FCSTD DOCUMENT  (FreeCAD 0.17R7529 (Git))
Label: extruder_body_hex_v1.4.1
License: CC-BY 3.0
LicenseURL: http://creativecommons.org/licenses/by/3.0/
objects: Sketcher::SketchObject×82, PartDesign::Pocket×48, PartDesign::Pad×30, Part::Feature×10, PartDesign::Chamfer×8, PartDesign::Fillet×4
note: 260 computed .brp shape members not serialized (recipe doc carries the construction recipe); baked Part::Feature solids carry a one-line shape summary decoded from their .brp

FEATURE [Sketcher::SketchObject] Sketch
  MapMode = 5
  sketch-geometry (56):
    g0: LineSegment [constr] StartX=38.5 StartY=7 StartZ=0 EndX=38.5 EndY=0 EndZ=0
    g1: LineSegment StartX=38.5 StartY=0 StartZ=0 EndX=-31.5 EndY=0 EndZ=0
    g2: LineSegment [constr] StartX=-31.5 StartY=0 StartZ=0 EndX=-31.5 EndY=7 EndZ=0
    g3: ArcOfCircle CenterX=-31.5 CenterY=3.5 CenterZ=0 NormalX=0 NormalY=0 NormalZ=1 Radius=3.5 StartAngle=1.5708 EndAngle=4.71239
    g4: LineSegment [constr] StartX=-31.5 StartY=7 StartZ=0 EndX=-35 EndY=7 EndZ=0
    g5: LineSegment [constr] StartX=-35 StartY=7 StartZ=0 EndX=-35 EndY=0 EndZ=0
    g6: LineSegment [constr] StartX=-35 StartY=0 StartZ=0 EndX=-31.5 EndY=0 EndZ=0
    g7: LineSegment [constr] StartX=38.5 StartY=7 StartZ=0 EndX=42 EndY=7 EndZ=0
    g8: LineSegment [constr] StartX=42 StartY=0 StartZ=0 EndX=38.5 EndY=0 EndZ=0
    g9: LineSegment StartX=-31.5 StartY=7 StartZ=0 EndX=-12.5 EndY=7 EndZ=0
    g10: ArcOfCircle CenterX=-12.5 CenterY=13 CenterZ=0 NormalX=0 NormalY=0 NormalZ=1 Radius=6 StartAngle=4.71239 EndAngle=6.28319
    g11: LineSegment [constr] StartX=-6.5 StartY=13 StartZ=0 EndX=-6.5 EndY=27 EndZ=0
    g12: LineSegment StartX=-6.5 StartY=13 StartZ=0 EndX=-14.7934 EndY=17.0274 EndZ=0
    g13: LineSegment StartX=-6.5 StartY=27 StartZ=0 EndX=-12.5 EndY=27 EndZ=0
    g14: ArcOfCircle CenterX=-12.5 CenterY=21.75 CenterZ=0 NormalX=0 NormalY=0 NormalZ=1 Radius=5.25 StartAngle=1.5708 EndAngle=4.26031
    g15: LineSegment StartX=-6.5 StartY=27 StartZ=0 EndX=-6.5 EndY=56 EndZ=0
    g16: ArcOfCircle CenterX=-0.5 CenterY=56 CenterZ=0 NormalX=0 NormalY=0 NormalZ=1 Radius=6 StartAngle=1.5708 EndAngle=3.14159
    g17: LineSegment StartX=-0.499999 StartY=62 StartZ=0 EndX=17.5 EndY=62 EndZ=0
    g18: LineSegment [constr] StartX=17.5 StartY=62 StartZ=0 EndX=17.5 EndY=7 EndZ=0
    g19: LineSegment [constr] StartX=17.5 StartY=7 StartZ=0 EndX=38.5 EndY=7 EndZ=0
    g20: LineSegment StartX=17.5 StartY=26.5 StartZ=0 EndX=28 EndY=26.5 EndZ=0
    g21: LineSegment StartX=28 StartY=26.5 StartZ=0 EndX=34 EndY=7 EndZ=0
    g22: ArcOfCircle CenterX=23.5 CenterY=13 CenterZ=0 NormalX=0 NormalY=0 NormalZ=1 Radius=6 StartAngle=3.14159 EndAngle=4.71239
    g23: ArcOfCircle CenterX=38 CenterY=17.75 CenterZ=0 NormalX=0 NormalY=0 NormalZ=1 Radius=2 StartAngle=1.5708 EndAngle=4.71239
    g24: LineSegment StartX=38 StartY=19.75 StartZ=0 EndX=41 EndY=19.75 EndZ=0
    g25: LineSegment [constr] StartX=41 StartY=19.75 StartZ=0 EndX=41 EndY=15.75 EndZ=0
    g26: LineSegment StartX=41 StartY=15.75 StartZ=0 EndX=38 EndY=15.75 EndZ=0
    g27: LineSegment [constr] StartX=38 StartY=15.75 StartZ=0 EndX=38 EndY=19.75 EndZ=0
    g28: ArcOfCircle CenterX=41 CenterY=17.75 CenterZ=0 NormalX=0 NormalY=0 NormalZ=1 Radius=2 StartAngle=4.71239 EndAngle=7.85398
    g29: LineSegment [constr] StartX=42 StartY=7 StartZ=0 EndX=42 EndY=3.5 EndZ=0
    g30: ArcOfCircle CenterX=38.5 CenterY=3.5 CenterZ=0 NormalX=0 NormalY=0 NormalZ=1 Radius=3.5 StartAngle=4.71239 EndAngle=6.28319
    g31: LineSegment [constr] StartX=42 StartY=3.5 StartZ=0 EndX=42 EndY=0 EndZ=0
    g32: LineSegment StartX=23.5 StartY=7 StartZ=0 EndX=34 EndY=7 EndZ=0
    g33: LineSegment StartX=17.5 StartY=26.5 StartZ=0 EndX=17.5 EndY=13 EndZ=0
    g34: ArcOfCircle CenterX=41 CenterY=17.75 CenterZ=0 NormalX=0 NormalY=0 NormalZ=1 Radius=4.6 StartAngle=6.02539 EndAngle=7.5456
    g35: LineSegment StartX=42 StartY=3.5 StartZ=0 EndX=45.448 EndY=16.5772 EndZ=0
    g36: LineSegment StartX=25.1292 StartY=47.3792 StartZ=0 EndX=28.1292 EndY=47.3792 EndZ=0
    g37: LineSegment [constr] StartX=28.1292 StartY=47.3792 StartZ=0 EndX=28.1292 EndY=43.3792 EndZ=0
    g38: LineSegment StartX=28.1292 StartY=43.3792 StartZ=0 EndX=25.1292 EndY=43.3792 EndZ=0
    g39: LineSegment [constr] StartX=25.1292 StartY=43.3792 StartZ=0 EndX=25.1292 EndY=47.3792 EndZ=0
    g40: ArcOfCircle CenterX=25.1292 CenterY=45.3792 CenterZ=0 NormalX=0 NormalY=0 NormalZ=1 Radius=2 StartAngle=1.5708 EndAngle=4.71239
    g41: ArcOfCircle CenterX=28.1292 CenterY=45.3792 CenterZ=0 NormalX=0 NormalY=0 NormalZ=1 Radius=2 StartAngle=4.71239 EndAngle=7.85398
    g42: LineSegment [constr] StartX=25.1292 StartY=45.3792 StartZ=0 EndX=38 EndY=17.75 EndZ=0
    g43: LineSegment StartX=52.7584 StartY=60.25 StartZ=0 EndX=55.7584 EndY=60.25 EndZ=0
    g44: LineSegment [constr] StartX=55.7584 StartY=60.25 StartZ=0 EndX=55.7584 EndY=56.25 EndZ=0
    g45: LineSegment StartX=55.7584 StartY=56.25 StartZ=0 EndX=52.7584 EndY=56.25 EndZ=0
    g46: LineSegment [constr] StartX=52.7584 StartY=56.25 StartZ=0 EndX=52.7584 EndY=60.25 EndZ=0
    g47: ArcOfCircle CenterX=52.7584 CenterY=58.25 CenterZ=0 NormalX=0 NormalY=0 NormalZ=1 Radius=2 StartAngle=1.5708 EndAngle=4.71239
    g48: ArcOfCircle CenterX=55.7584 CenterY=58.25 CenterZ=0 NormalX=0 NormalY=0 NormalZ=1 Radius=2 StartAngle=4.71239 EndAngle=7.85398
    g49: LineSegment [constr] StartX=25.1292 StartY=45.3792 StartZ=0 EndX=52.7584 EndY=58.25 EndZ=0
    g50: Circle [constr] CenterX=55.7584 CenterY=58.25 CenterZ=0 NormalX=0 NormalY=0 NormalZ=1 Radius=6.3
    g51: ArcOfCircle [constr] CenterX=28.1292 CenterY=45.3792 CenterZ=0 NormalX=0 NormalY=0 NormalZ=1 Radius=4.6 StartAngle=4.51582 EndAngle=6.99813
    g52: Circle [constr] CenterX=47.2887 CenterY=37.492 CenterZ=0 NormalX=0 NormalY=0 NormalZ=1 Radius=16.1194
    g53: ArcOfCircle CenterX=47.2887 CenterY=37.492 CenterZ=0 NormalX=0 NormalY=0 NormalZ=1 Radius=16.1194 StartAngle=1.18339 EndAngle=4.40401
    g54: ArcOfCircle CenterX=55.7584 CenterY=58.25 CenterZ=0 NormalX=0 NormalY=0 NormalZ=1 Radius=6.3 StartAngle=4.32499 EndAngle=7.98709
    g55: ArcOfCircle CenterX=17.5 CenterY=343.976 CenterZ=0 NormalX=0 NormalY=0 NormalZ=1 Radius=281.976 StartAngle=4.71239 EndAngle=4.8455
  constraints (168):
    c: Coincident(g0,g1)
    c: Coincident(g1,g2)
    c: Horizontal(g1)
    c: Vertical(g0)
    c: Vertical(g2)
    c: PointOnObject(g3,g2)
    c: Coincident(g3,g1)
    c: DistanceY(g2,g1) = -7
    c: PointOnObject(g1,g-1)
    c: Coincident(g4,g5)
    c: Coincident(g5,g6)
    c: Horizontal(g4)
    c: Horizontal(g6)
    c: Vertical(g5)
    c: Coincident(g6,g1)
    c: Tangent(g5,g3)
    c: Horizontal(g7)
    c: Horizontal(g8)
    c: Coincident(g8,g0)
    c: DistanceX(g8,g5) = -77
    c: DistanceX(g-1,g8) = 42
    c: Coincident(g9,g2)
    c: Horizontal(g9)
    c: Coincident(g3,g2)
    c: Coincident(g10,g9)
    c: Radius(g10) = 6
    c: Tangent(g10,g9)
    c: Coincident(g11,g10)
    c: Vertical(g11)
    c: Tangent(g10,g11)
    c: Coincident(g12,g10)
    c: Coincident(g13,g11)
    c: Horizontal(g13)
    c: DistanceY(g11,g9) = -20
    c: DistanceX(g-1,g13) = -12.5
    c: DistanceX(g11,g4) = -28.5
    c: Coincident(g14,g13)
    c: Coincident(g14,g12)
    c: Tangent(g14,g13)
    c: Tangent(g14,g12)
    c: Radius(g14) = 5.25
    c: Coincident(g7,g0)
    c: Coincident(g15,g11)
    c: Vertical(g15)
    c: Coincident(g16,g15)
    c: Radius(g16) = 6
    c: Tangent(g16,g15)
    c: Coincident(g17,g16)
    c: Horizontal(g17)
    c: DistanceY(g1,g16) = 62
    c: Vertical(g18)
    c: Coincident(g17,g18)
    c: DistanceX(g18,g7) = 24.5
    c: Coincident(g19,g18)
    c: Coincident(g19,g0)
    c: Horizontal(g19)
    c: PointOnObject(g20,g18)
    c: Horizontal(g20)
    c: Coincident(g21,g20)
    c: PointOnObject(g21,g19)
    c: DistanceX(g21,g7) = 8
    c: PointOnObject(g22,g18)
    c: PointOnObject(g22,g19)
    c: Radius(g22) = 6
    c: Tangent(g22,g19)
    c: Tangent(g22,g18)
    c: DistanceX(g20) = 10.5
    c: DistanceY(g20,g8) = -26.5
    c: Tangent(g16,g17)
    c: Coincident(g4,g2)
    c: Coincident(g24,g25)
    c: Coincident(g25,g26)
    c: Coincident(g26,g27)
    c: Coincident(g27,g24)
    c: Horizontal(g24)
    c: Horizontal(g26)
    c: Vertical(g25)
    c: Vertical(g27)
    c: Coincident(g24,g23)
    c: PointOnObject(g23,g27)
    c: Coincident(g23,g26)
    c: PointOnObject(g28,g25)
    c: Coincident(g28,g24)
    c: Coincident(g28,g25)
    c: DistanceX(g24) = 3
    c: DistanceY(g27) = 4
    c: DistanceY(g25,g8) = -15.75
    c: DistanceX(g-1,g23) = 38
    c: Vertical(g29)
    c: PointOnObject(g30,g0)
    c: Coincident(g30,g0)
    c: Coincident(g30,g29)
    c: Radius(g30) = 3.5
    c: Tangent(g30,g29)
    c: Coincident(g29,g7)
    c: Coincident(g31,g29)
    c: Coincident(g31,g8)
    c: Vertical(g31)
    c: DistanceY(g7,g8) = -7
    c: Coincident(g32,g22)
    c: Coincident(g32,g21)
    c: Coincident(g33,g20)
    c: Coincident(g33,g22)
    c: Coincident(g34,g28)
    c: Radius(g34) = 4.6
    c: Coincident(g35,g29)
    c: Coincident(g35,g34)
    c: Tangent(g35,g34)
    c: Coincident(g36,g37)
    c: Coincident(g37,g38)
    c: Coincident(g38,g39)
    c: Coincident(g39,g36)
    c: Horizontal(g36)
    c: Horizontal(g38)
    c: Vertical(g37)
    c: Vertical(g39)
    c: DistanceY(g39) = 4
    c: DistanceX(g38) = -3
    c: PointOnObject(g40,g39)
    c: Coincident(g40,g36)
    c: Coincident(g40,g38)
    c: PointOnObject(g41,g37)
    c: Coincident(g41,g36)
    c: Coincident(g41,g37)
    c: Coincident(g42,g40)
    c: Coincident(g42,g23)
    c: Coincident(g43,g44)
    c: Coincident(g44,g45)
    c: Coincident(g45,g46)
    c: Coincident(g46,g43)
    c: Horizontal(g43)
    c: Horizontal(g45)
    c: Vertical(g44)
    c: Vertical(g46)
    c: DistanceX(g45) = -3
    c: DistanceY(g46) = 4
    c: PointOnObject(g47,g46)
    c: Coincident(g47,g43)
    c: Coincident(g47,g45)
    c: PointOnObject(g48,g44)
    c: Coincident(g48,g43)
    c: Coincident(g48,g44)
    c: Distance(g42) = 30.48
    c: Coincident(g49,g40)
    c: Coincident(g49,g47)
    c: Perpendicular(g49,g42)
    c: Distance(g49) = 30.48
    c: DistanceY(g-1,g48) = 58.25
    c: Coincident(g50,g48)
    c: Radius(g50) = 6.3
    c: Coincident(g51,g41)
    c: PointOnObject(g51,g49)
    c: PointOnObject(g51,g42)
    c: Radius(g51) = 4.6
    c: Tangent(g52,g50)
    c: Tangent(g52,g34)
    c: Tangent(g52,g51)
    c: Coincident(g53,g52)
    c: PointOnObject(g53,g34)
    c: Equal(g53,g52)
    c: Coincident(g53,g34)
    c: Coincident(g54,g48)
    c: Coincident(g54,g53)
    c: Coincident(g55,g17)
    c: Coincident(g55,g54)
    c: Tangent(g55,g17)
    c: Radius(g54) = 6.3
    c: Tangent(g55,g50)
FEATURE [PartDesign::Pad] Pad
  Length = 9.5
  Length2 = 100
  Profile = -> Sketch
  Type = 0
FEATURE [Sketcher::SketchObject] Sketch001
  ExternalGeometry = -> [Pad]
  MapMode = 5
  Placement = pos=(0,0,9.5) rot=(0,0,1;0rad)
  Support = -> [Pad]
  sketch-geometry (4):
    g0: LineSegment StartX=10.2 StartY=50.625 StartZ=0 EndX=-6.5 EndY=50.625 EndZ=0
    g1: LineSegment StartX=-6.5 StartY=50.625 StartZ=0 EndX=-6.5 EndY=62 EndZ=0
    g2: LineSegment StartX=-6.5 StartY=62 StartZ=0 EndX=10.2 EndY=62 EndZ=0
    g3: LineSegment StartX=10.2 StartY=62 StartZ=0 EndX=10.2 EndY=50.625 EndZ=0
  constraints (12):
    c: Coincident(g0,g1)
    c: Coincident(g1,g2)
    c: Coincident(g2,g3)
    c: Coincident(g3,g0)
    c: Horizontal(g0)
    c: Horizontal(g2)
    c: Vertical(g1)
    c: Vertical(g3)
    c: PointOnObject(g1,g-3)
    c: PointOnObject(g1,g-4)
    c: DistanceX(g0) = -16.7
    c: DistanceY(g3) = -11.375
FEATURE [PartDesign::Pocket] Pocket
  Length = 4
  Profile = -> Sketch001
  Type = 0
FEATURE [Sketcher::SketchObject] Sketch002
  ExternalGeometry = -> [Pocket]
  MapMode = 5
  Placement = pos=(0,0,9.5) rot=(0,0,1;0rad)
  Support = -> [Pocket]
  sketch-geometry (17):
    g0: LineSegment StartX=17.5 StartY=62 StartZ=0 EndX=17.5 EndY=13 EndZ=0
    g1: LineSegment StartX=17.5 StartY=62 StartZ=0 EndX=10.2 EndY=62 EndZ=0
    g2: ArcOfCircle CenterX=23.5 CenterY=13 CenterZ=0 NormalX=0 NormalY=0 NormalZ=1 Radius=6 StartAngle=3.14159 EndAngle=4.71239
    g3: ArcOfCircle CenterX=38.5 CenterY=3.5 CenterZ=0 NormalX=0 NormalY=0 NormalZ=1 Radius=3.5 StartAngle=4.71238 EndAngle=7.85399
    g4: LineSegment StartX=23.5 StartY=7 StartZ=0 EndX=38.5 EndY=7 EndZ=0
    g5: LineSegment [constr] StartX=38.5 StartY=7 StartZ=0 EndX=38.5 EndY=5.6e-11 EndZ=0
    g6: LineSegment StartX=38.5 StartY=5.6e-11 StartZ=0 EndX=-31.5 EndY=0 EndZ=0
    g7: ArcOfCircle CenterX=-31.5 CenterY=3.5 CenterZ=0 NormalX=0 NormalY=0 NormalZ=1 Radius=3.5 StartAngle=1.5708 EndAngle=4.71239
    g8: LineSegment [constr] StartX=-31.5 StartY=7 StartZ=0 EndX=-31.5 EndY=0 EndZ=0
    g9: LineSegment StartX=-12.5 StartY=7 StartZ=0 EndX=-31.5 EndY=7 EndZ=0
    g10: ArcOfCircle CenterX=-12.5 CenterY=13 CenterZ=0 NormalX=0 NormalY=0 NormalZ=1 Radius=6 StartAngle=4.71239 EndAngle=6.28319
    g11: LineSegment StartX=-6.5 StartY=13 StartZ=0 EndX=-14.7934 EndY=17.0274 EndZ=0
    g12: LineSegment StartX=-12.5 StartY=27 StartZ=0 EndX=-6.5 EndY=27 EndZ=0
    g13: LineSegment StartX=-6.5 StartY=27 StartZ=0 EndX=-6.5 EndY=50.625 EndZ=0
    g14: LineSegment StartX=-6.5 StartY=50.625 StartZ=0 EndX=10.2 EndY=50.625 EndZ=0
    g15: LineSegment StartX=10.2 StartY=50.625 StartZ=0 EndX=10.2 EndY=62 EndZ=0
    g16: ArcOfCircle CenterX=-12.5 CenterY=21.75 CenterZ=0 NormalX=0 NormalY=0 NormalZ=1 Radius=5.25 StartAngle=1.5708 EndAngle=4.26031
  constraints (44):
    c: Coincident(g1,g0)
    c: Coincident(g1,g-3)
    c: Coincident(g0,g-3)
    c: Coincident(g0,g-4)
    c: Coincident(g2,g0)
    c: Coincident(g2,g-5)
    c: Tangent(g2,g0)
    c: Coincident(g3,g-6)
    c: Coincident(g4,g2)
    c: Coincident(g4,g3)
    c: Horizontal(g4)
    c: Coincident(g5,g3)
    c: Coincident(g5,g3)
    c: Vertical(g5)
    c: Radius(g3) = 3.5
    c: Coincident(g6,g3)
    c: Coincident(g6,g-6)
    c: Coincident(g7,g6)
    c: Radius(g7) = 3.5
    c: Coincident(g8,g7)
    c: Coincident(g8,g6)
    c: Vertical(g8)
    c: PointOnObject(g7,g8)
    c: Coincident(g9,g7)
    c: Coincident(g9,g-7)
    c: Coincident(g10,g9)
    c: Coincident(g10,g-7)
    c: Coincident(g10,g-7)
    c: Coincident(g11,g10)
    c: Coincident(g13,g12)
    c: Horizontal(g14)
    c: Coincident(g15,g14)
    c: Coincident(g15,g1)
    c: Vertical(g15)
    c: Coincident(g13,g14)
    c: Coincident(g-8,g14)
    c: Coincident(g-9,g12)
    c: Coincident(g11,g-9)
    c: Horizontal(g12)
    c: Coincident(g16,g-9)
    c: Coincident(g16,g12)
    c: Coincident(g11,g16)
    c: Coincident(g12,g-10)
    c: Coincident(g13,g-10)
FEATURE [PartDesign::Pad] Pad001
  Length = 18.5
  Length2 = 100
  Profile = -> Sketch002
  Type = 0
FEATURE [Sketcher::SketchObject] Sketch003
  ExternalGeometry = -> [Pad001]
  MapMode = 5
  Placement = pos=(0,0,28) rot=(0,0,1;0rad)
  Support = -> [Pad001]
  sketch-geometry (1):
    g0: Circle CenterX=4.6 CenterY=38 CenterZ=0 NormalX=0 NormalY=0 NormalZ=1 Radius=4.4
  constraints (3):
    c: DistanceX(g0,g-3) = -11.1
    c: Radius(g0) = 4.4
    c: DistanceY(g-1,g0) = 38
FEATURE [PartDesign::Pocket] Pocket001
  Length = 19.68
  Profile = -> Sketch003
  Type = 0
FEATURE [Sketcher::SketchObject] Sketch004
  ExternalGeometry = -> [Pocket001]
  MapMode = 5
  Placement = pos=(0,0,28) rot=(0,0,1;0rad)
  Support = -> [Pocket001]
  sketch-geometry (10):
    g0: Circle [constr] CenterX=-8.51624 CenterY=37.5745 CenterZ=0 NormalX=0 NormalY=0 NormalZ=1 Radius=11.3
    g1: LineSegment [constr] StartX=0 StartY=34.2576 StartZ=0 EndX=2.286 EndY=34.2576 EndZ=0
    g2: LineSegment StartX=-104.987 StartY=0 StartZ=0 EndX=-84.2591 EndY=0 EndZ=0
    g3: LineSegment [constr] StartX=5.5 StartY=34.2576 StartZ=0 EndX=-6.5 EndY=34.2576 EndZ=0
    g4: LineSegment StartX=5.5 StartY=50.625 StartZ=0 EndX=5.5 EndY=34.2576 EndZ=0
    g5: LineSegment StartX=5.5 StartY=50.625 StartZ=0 EndX=-6.5 EndY=50.625 EndZ=0
    g6: LineSegment [constr] StartX=-6.5 StartY=50.625 StartZ=0 EndX=-6.5 EndY=34.2576 EndZ=0
    g7: LineSegment StartX=2.286 StartY=34.2576 StartZ=0 EndX=5.5 EndY=34.2576 EndZ=0
    g8: ArcOfCircle CenterX=-8.51624 CenterY=37.5745 CenterZ=0 NormalX=0 NormalY=0 NormalZ=1 Radius=11.3 StartAngle=1.39141 EndAngle=5.98527
    g9: LineSegment StartX=-6.5 StartY=50.625 StartZ=0 EndX=-6.5 EndY=48.6931 EndZ=0
  constraints (27):
    c: Radius(g0) = 11.3
    c: PointOnObject(g1,g-2)
    c: Horizontal(g1)
    c: DistanceX(g1) = 2.286
    c: PointOnObject(g1,g0)
    c: Tangent(g2,g-1)
    c: PointOnObject(g-3,g0)
    c: Coincident(g4,g3)
    c: Horizontal(g3)
    c: Vertical(g4)
    c: PointOnObject(g1,g3)
    c: PointOnObject(g1,g-4)
    c: Coincident(g5,g4)
    c: Coincident(g5,g-5)
    c: Coincident(g6,g3)
    c: Coincident(g6,g5)
    c: Vertical(g6)
    c: Coincident(g7,g1)
    c: Coincident(g7,g3)
    c: PointOnObject(g4,g-5)
    c: DistanceX(g4,g-5) = 4.7
    c: Coincident(g8,g0)
    c: PointOnObject(g8,g6)
    c: PointOnObject(g8,g-4)
    c: Coincident(g8,g1)
    c: Coincident(g9,g5)
    c: Coincident(g9,g8)
FEATURE [PartDesign::Pocket] Pocket002
  Length = 18.5
  Profile = -> Sketch004
  Type = 0
FEATURE [Sketcher::SketchObject] Sketch005
  ExternalGeometry = -> [Pocket002]
  MapMode = 5
  Placement = pos=(0,0,28) rot=(0,0,1;0rad)
  Support = -> [Pocket002]
  sketch-geometry (1):
    g0: Circle CenterX=4.6 CenterY=38 CenterZ=0 NormalX=0 NormalY=0 NormalZ=1 Radius=8
  constraints (2):
    c: Coincident(g0,g-3)
    c: Radius(g0) = 8
FEATURE [PartDesign::Pocket] Pocket003
  Length = 9.5
  Profile = -> Sketch005
  Type = 0
FEATURE [Sketcher::SketchObject] Sketch006
  ExternalGeometry = -> [Pocket003]
  MapMode = 5
  Placement = pos=(0,0,28) rot=(0,0,1;0rad)
  Support = -> [Pocket003]
  sketch-geometry (1):
    g0: Circle CenterX=4.6 CenterY=38 CenterZ=0 NormalX=0 NormalY=0 NormalZ=1 Radius=11.3
  constraints (2):
    c: Coincident(g0,g-3)
    c: Radius(g0) = 11.3
FEATURE [PartDesign::Pocket] Pocket004
  Length = 8
  Profile = -> Sketch006
  Type = 0
FEATURE [Sketcher::SketchObject] Sketch007
  ExternalGeometry = -> [Pocket004]
  MapMode = 5
  Placement = pos=(0,0,8.32) rot=(0,0,1;0rad)
  Support = -> [Pocket004]
  sketch-geometry (1):
    g0: Circle CenterX=4.6 CenterY=38 CenterZ=0 NormalX=0 NormalY=0 NormalZ=1 Radius=4
  constraints (2):
    c: Coincident(g0,g-3)
    c: Radius(g0) = 4
FEATURE [PartDesign::Pocket] Pocket005
  Length = 0
  Profile = -> Sketch007
  Type = 1
FEATURE [Sketcher::SketchObject] Sketch008
  ExternalGeometry = -> [Pocket005]
  MapMode = 5
  Placement = pos=(0,0,0) rot=(1,0,0;3.14159rad)
  Support = -> [Pocket005]
  sketch-geometry (1):
    g0: Circle CenterX=4.6 CenterY=-38 CenterZ=0 NormalX=0 NormalY=0 NormalZ=1 Radius=11.3
  constraints (2):
    c: Coincident(g0,g-3)
    c: Radius(g0) = 11.3
FEATURE [PartDesign::Pocket] Pocket006
  Length = 8
  Profile = -> Sketch008
  Type = 0
FEATURE [PartDesign::Chamfer] Chamfer
  Base = -> Pocket006 [Edge22]
  Size = 1
FEATURE [PartDesign::Fillet] Fillet
  Base = -> Chamfer [Edge37,Edge40]
  Radius = 0.5
FEATURE [Sketcher::SketchObject] Sketch009
  ExternalGeometry = -> [Fillet]
  MapMode = 5
  Placement = pos=(0,0,28) rot=(0,0,1;0rad)
  Support = -> [Fillet]
  sketch-geometry (4):
    g0: LineSegment StartX=-6.5 StartY=13 StartZ=0 EndX=-17.75 EndY=13 EndZ=0
    g1: LineSegment StartX=-17.75 StartY=13 StartZ=0 EndX=-17.75 EndY=27 EndZ=0
    g2: LineSegment StartX=-17.75 StartY=27 StartZ=0 EndX=-6.5 EndY=27 EndZ=0
    g3: LineSegment StartX=-6.5 StartY=27 StartZ=0 EndX=-6.5 EndY=13 EndZ=0
  constraints (11):
    c: Coincident(g0,g1)
    c: Coincident(g1,g2)
    c: Coincident(g2,g3)
    c: Coincident(g3,g0)
    c: Horizontal(g0)
    c: Horizontal(g2)
    c: Vertical(g1)
    c: Vertical(g3)
    c: Coincident(g0,g-3)
    c: Tangent(g2,g-4)
    c: Tangent(g1,g-4)
FEATURE [PartDesign::Pocket] Pocket007
  Length = 7.75
  Profile = -> Sketch009
  Type = 0
FEATURE [Sketcher::SketchObject] Sketch010
  ExternalGeometry = -> [Pocket007]
  MapMode = 5
  Placement = pos=(0,0,20.25) rot=(0,0,1;0rad)
  Support = -> [Pocket007]
  sketch-geometry (1):
    g0: Circle CenterX=-12.5 CenterY=21.75 CenterZ=0 NormalX=0 NormalY=0 NormalZ=1 Radius=3.3
  constraints (2):
    c: Coincident(g0,g-3)
    c: Radius(g0) = 3.3
FEATURE [PartDesign::Pocket] Pocket008
  Length = 0.75
  Profile = -> Sketch010
  Type = 0
FEATURE [Sketcher::SketchObject] Sketch011
  ExternalGeometry = -> [Pocket008]
  MapMode = 5
  Placement = pos=(0,0,19.5) rot=(0,0,1;0rad)
  Support = -> [Pocket008]
  sketch-geometry (1):
    g0: Circle CenterX=-12.5 CenterY=21.75 CenterZ=0 NormalX=0 NormalY=0 NormalZ=1 Radius=1.95
  constraints (2):
    c: Coincident(g0,g-3)
    c: Radius(g0) = 1.95
FEATURE [PartDesign::Pocket] Pocket009
  Length = 5
  Profile = -> Sketch011
  Type = 1
FEATURE [Sketcher::SketchObject] Sketch012
  ExternalGeometry = -> [Pocket009]
  MapMode = 5
  Placement = pos=(0,0,0) rot=(1,0,0;3.14159rad)
  Support = -> [Pocket009]
  sketch-geometry (4):
    g0: LineSegment StartX=-6.5 StartY=-13 StartZ=0 EndX=-17.75 EndY=-13 EndZ=0
    g1: LineSegment StartX=-17.75 StartY=-13 StartZ=0 EndX=-17.75 EndY=-27 EndZ=0
    g2: LineSegment StartX=-17.75 StartY=-27 StartZ=0 EndX=-6.5 EndY=-27 EndZ=0
    g3: LineSegment StartX=-6.5 StartY=-27 StartZ=0 EndX=-6.5 EndY=-13 EndZ=0
  constraints (11):
    c: Coincident(g0,g1)
    c: Coincident(g1,g2)
    c: Coincident(g2,g3)
    c: Coincident(g3,g0)
    c: Horizontal(g0)
    c: Horizontal(g2)
    c: Vertical(g1)
    c: Vertical(g3)
    c: Coincident(g0,g-4)
    c: Tangent(g1,g-3)
    c: Coincident(g2,g-5)
FEATURE [PartDesign::Pocket] Pocket010
  Length = 8.32
  Profile = -> Sketch012
  Type = 0
FEATURE [Sketcher::SketchObject] Sketch013
  ExternalGeometry = -> [Pocket010]
  MapMode = 5
  Placement = pos=(0,0,0) rot=(1,0,0;3.14159rad)
  Support = -> [Pocket010]
  sketch-geometry (21):
    g0: ArcOfCircle CenterX=38 CenterY=-17.75 CenterZ=0 NormalX=0 NormalY=0 NormalZ=1 Radius=3.8 StartAngle=1.5708 EndAngle=4.71239
    g1: ArcOfCircle CenterX=41 CenterY=-17.75 CenterZ=0 NormalX=0 NormalY=0 NormalZ=1 Radius=3.8 StartAngle=4.71239 EndAngle=7.85398
    g2: ArcOfCircle CenterX=25.1292 CenterY=-45.3792 CenterZ=0 NormalX=0 NormalY=0 NormalZ=1 Radius=3.8 StartAngle=1.5708 EndAngle=4.71239
    g3: ArcOfCircle CenterX=28.1292 CenterY=-45.3792 CenterZ=0 NormalX=0 NormalY=0 NormalZ=1 Radius=3.8 StartAngle=4.71239 EndAngle=7.85398
    g4: ArcOfCircle CenterX=52.7584 CenterY=-58.25 CenterZ=0 NormalX=0 NormalY=0 NormalZ=1 Radius=3.8 StartAngle=1.5708 EndAngle=4.71239
    g5: ArcOfCircle CenterX=55.7584 CenterY=-58.25 CenterZ=0 NormalX=0 NormalY=0 NormalZ=1 Radius=3.8 StartAngle=4.71239 EndAngle=7.85398
    g6: LineSegment StartX=52.7584 StartY=-54.45 StartZ=0 EndX=55.7584 EndY=-54.45 EndZ=0
    g7: LineSegment StartX=52.7584 StartY=-62.05 StartZ=0 EndX=55.7584 EndY=-62.05 EndZ=0
    g8: LineSegment StartX=25.1292 StartY=-49.1792 StartZ=0 EndX=28.1292 EndY=-49.1792 EndZ=0
    g9: LineSegment StartX=25.1292 StartY=-41.5792 StartZ=0 EndX=28.1292 EndY=-41.5792 EndZ=0
    g10: LineSegment StartX=38 StartY=-21.55 StartZ=0 EndX=41 EndY=-21.55 EndZ=0
    g11: LineSegment StartX=38 StartY=-13.95 StartZ=0 EndX=41 EndY=-13.95 EndZ=0
    g12: LineSegment [constr] StartX=41 StartY=-19.75 StartZ=0 EndX=41 EndY=-21.55 EndZ=0
    g13: LineSegment [constr] StartX=38 StartY=-15.75 StartZ=0 EndX=38 EndY=-13.95 EndZ=0
    g14: LineSegment [constr] StartX=28.1292 StartY=-41.5792 StartZ=0 EndX=28.1292 EndY=-43.3792 EndZ=0
    g15: LineSegment [constr] StartX=25.1292 StartY=-47.3792 StartZ=0 EndX=25.1292 EndY=-49.1792 EndZ=0
    g16: LineSegment [constr] StartX=55.7584 StartY=-54.45 StartZ=0 EndX=55.7584 EndY=-56.25 EndZ=0
    g17: LineSegment [constr] StartX=52.7584 StartY=-60.25 StartZ=0 EndX=52.7584 EndY=-62.05 EndZ=0
    g18: LineSegment [constr] StartX=38 StartY=-19.75 StartZ=0 EndX=38 EndY=-21.55 EndZ=0
    g19: LineSegment [constr] StartX=25.1292 StartY=-43.3792 StartZ=0 EndX=25.1292 EndY=-41.5792 EndZ=0
    g20: LineSegment [constr] StartX=28.1292 StartY=-47.3792 StartZ=0 EndX=28.1292 EndY=-49.1792 EndZ=0
  constraints (54):
    c: Coincident(g0,g-7)
    c: Coincident(g1,g-8)
    c: Coincident(g2,g-3)
    c: Coincident(g3,g-4)
    c: Coincident(g4,g-5)
    c: Coincident(g5,g-6)
    c: Coincident(g6,g4)
    c: Coincident(g6,g5)
    c: Horizontal(g6)
    c: Coincident(g7,g4)
    c: Coincident(g7,g5)
    c: Horizontal(g7)
    c: Coincident(g8,g2)
    c: Coincident(g8,g3)
    c: Horizontal(g8)
    c: Coincident(g9,g2)
    c: Coincident(g9,g3)
    c: Horizontal(g9)
    c: Coincident(g10,g0)
    c: Coincident(g10,g1)
    c: Horizontal(g10)
    c: Coincident(g11,g0)
    c: Coincident(g11,g1)
    c: Horizontal(g11)
    c: Coincident(g12,g-8)
    c: Coincident(g12,g1)
    c: Vertical(g12)
    c: Coincident(g13,g-7)
    c: Coincident(g13,g0)
    c: Vertical(g13)
    c: Coincident(g14,g3)
    c: Vertical(g14)
    c: Coincident(g15,g-3)
    c: Coincident(g15,g2)
    c: Vertical(g15)
    c: Coincident(g14,g-4)
    c: Radius(g1) = 3.8
    c: Radius(g3) = 3.8
    c: Coincident(g16,g5)
    c: Coincident(g16,g-6)
    c: Vertical(g16)
    c: Coincident(g17,g-5)
    c: Coincident(g17,g4)
    c: Vertical(g17)
    c: Radius(g5) = 3.8
    c: Coincident(g18,g-7)
    c: Vertical(g18)
    c: Tangent(g4,g6)
    c: Coincident(g19,g-3)
    c: Coincident(g19,g2)
    c: Vertical(g19)
    c: Coincident(g20,g-4)
    c: Coincident(g20,g3)
    c: Coincident(g18,g0)
FEATURE [PartDesign::Pocket] Pocket011
  Length = 1.5
  Profile = -> Sketch013
  Type = 0
FEATURE [PartDesign::Chamfer] Chamfer001
  Base = -> Pocket011 [Edge173]
  Size = 1.6
FEATURE [PartDesign::Chamfer] Chamfer002
  Base = -> Chamfer001 [Edge169]
  Size = 1.6
FEATURE [PartDesign::Chamfer] Chamfer003
  Base = -> Chamfer002 [Edge73]
  Size = 1.6
FEATURE [Sketcher::SketchObject] Sketch015
  ExternalGeometry = -> [Chamfer003]
  MapMode = 5
  Placement = pos=(10.2,0,0) rot=(0.57735,-0.57735,-0.57735;2.0944rad)
  Support = -> [Chamfer003]
  sketch-geometry (18):
    g0: LineSegment StartX=-55.825 StartY=25.7 StartZ=0 EndX=-50.175 EndY=25.7 EndZ=0
    g1: LineSegment [constr] StartX=-50.175 StartY=25.7 StartZ=0 EndX=-50.175 EndY=18.3 EndZ=0
    g2: LineSegment StartX=-50.175 StartY=18.3 StartZ=0 EndX=-55.825 EndY=18.3 EndZ=0
    g3: LineSegment [constr] StartX=-55.825 StartY=18.3 StartZ=0 EndX=-55.825 EndY=25.7 EndZ=0
    g4: LineSegment StartX=-55.825 StartY=9.9 StartZ=0 EndX=-50.175 EndY=9.9 EndZ=0
    g5: LineSegment [constr] StartX=-50.175 StartY=9.9 StartZ=0 EndX=-50.175 EndY=2.5 EndZ=0
    g6: LineSegment StartX=-50.175 StartY=2.5 StartZ=0 EndX=-55.825 EndY=2.5 EndZ=0
    g7: LineSegment [constr] StartX=-55.825 StartY=2.5 StartZ=0 EndX=-55.825 EndY=9.9 EndZ=0
    g8: LineSegment StartX=-55.825 StartY=25.7 StartZ=0 EndX=-57.675 EndY=22 EndZ=0
    g9: LineSegment StartX=-57.675 StartY=22 StartZ=0 EndX=-55.825 EndY=18.3 EndZ=0
    g10: LineSegment StartX=-50.175 StartY=25.7 StartZ=0 EndX=-48.325 EndY=22 EndZ=0
    g11: LineSegment StartX=-50.175 StartY=18.3 StartZ=0 EndX=-48.325 EndY=22 EndZ=0
    g12: LineSegment [constr] StartX=-57.675 StartY=22 StartZ=0 EndX=-48.325 EndY=22 EndZ=0
    g13: LineSegment StartX=-55.825 StartY=9.9 StartZ=0 EndX=-57.675 EndY=6.2 EndZ=0
    g14: LineSegment StartX=-57.675 StartY=6.2 StartZ=0 EndX=-55.825 EndY=2.5 EndZ=0
    g15: LineSegment StartX=-50.175 StartY=9.9 StartZ=0 EndX=-48.325 EndY=6.2 EndZ=0
    g16: LineSegment StartX=-50.175 StartY=2.5 StartZ=0 EndX=-48.325 EndY=6.2 EndZ=0
    g17: LineSegment [constr] StartX=-57.675 StartY=6.2 StartZ=0 EndX=-48.325 EndY=6.2 EndZ=0
  constraints (48):
    c: Coincident(g0,g1)
    c: Coincident(g1,g2)
    c: Coincident(g2,g3)
    c: Coincident(g3,g0)
    c: Horizontal(g0)
    c: Horizontal(g2)
    c: Vertical(g1)
    c: Vertical(g3)
    c: Coincident(g4,g5)
    c: Coincident(g5,g6)
    c: Coincident(g6,g7)
    c: Coincident(g7,g4)
    c: Horizontal(g4)
    c: Horizontal(g6)
    c: Vertical(g5)
    c: Vertical(g7)
    c: PointOnObject(g2,g7)
    c: PointOnObject(g1,g5)
    c: DistanceY(g0,g-3) = 2.3
    c: Coincident(g8,g0)
    c: Coincident(g9,g8)
    c: Coincident(g9,g2)
    c: Coincident(g10,g0)
    c: Coincident(g11,g1)
    c: Coincident(g11,g10)
    c: Coincident(g12,g8)
    c: Coincident(g12,g10)
    c: Horizontal(g12)
    c: Symmetric(g0,g2,g12)
    c: DistanceX(g12) = 9.35
    c: Parallel(g9,g10)
    c: DistanceX(g2) = -5.65
    c: Coincident(g13,g4)
    c: Coincident(g14,g13)
    c: Coincident(g14,g6)
    c: Coincident(g15,g4)
    c: Coincident(g16,g5)
    c: Coincident(g16,g15)
    c: Coincident(g17,g13)
    c: Coincident(g17,g15)
    c: Horizontal(g17)
    c: Symmetric(g4,g6,g17)
    c: DistanceX(g17) = 9.35
    c: DistanceY(g1) = -7.4
    c: DistanceY(g4,g2) = 8.4
    c: DistanceY(g5) = -7.4
    c: Parallel(g8,g13)
    c: DistanceX(g0,g-3) = -6.175
FEATURE [PartDesign::Pocket] Pocket012
  Length = 5.5
  Profile = -> Sketch015
  Type = 0
FEATURE [Sketcher::SketchObject] Sketch016
  ExternalGeometry = -> [Pocket012]
  MapMode = 5
  Placement = pos=(0,0,0) rot=(1,0,0;3.14159rad)
  Support = -> [Pocket012]
  sketch-geometry (10):
    g0: ArcOfCircle CenterX=28.1292 CenterY=-45.3792 CenterZ=0 NormalX=0 NormalY=0 NormalZ=1 Radius=4 StartAngle=4.71239 EndAngle=7.85398
    g1: ArcOfCircle CenterX=28.1292 CenterY=-45.3792 CenterZ=0 NormalX=0 NormalY=0 NormalZ=1 Radius=3.6 StartAngle=4.71239 EndAngle=7.85398
    g2: LineSegment [constr] StartX=28.1292 StartY=-41.3792 StartZ=0 EndX=28.1292 EndY=-49.3792 EndZ=0
    g3: ArcOfCircle CenterX=25.1292 CenterY=-45.3792 CenterZ=0 NormalX=0 NormalY=0 NormalZ=1 Radius=4 StartAngle=1.5708 EndAngle=4.71239
    g4: ArcOfCircle CenterX=25.1292 CenterY=-45.3792 CenterZ=0 NormalX=0 NormalY=0 NormalZ=1 Radius=3.6 StartAngle=1.5708 EndAngle=4.71239
    g5: LineSegment [constr] StartX=25.1292 StartY=-41.3792 StartZ=0 EndX=25.1292 EndY=-49.3792 EndZ=0
    g6: LineSegment StartX=25.1292 StartY=-41.3792 StartZ=0 EndX=28.1292 EndY=-41.3792 EndZ=0
    g7: LineSegment StartX=25.1292 StartY=-41.7792 StartZ=0 EndX=28.1292 EndY=-41.7792 EndZ=0
    g8: LineSegment StartX=25.1292 StartY=-48.9792 StartZ=0 EndX=28.1292 EndY=-48.9792 EndZ=0
    g9: LineSegment StartX=25.1292 StartY=-49.3792 StartZ=0 EndX=28.1292 EndY=-49.3792 EndZ=0
  constraints (28):
    c: Coincident(g0,g-4)
    c: Coincident(g1,g0)
    c: Coincident(g2,g0)
    c: Coincident(g2,g0)
    c: Vertical(g2)
    c: PointOnObject(g0,g2)
    c: PointOnObject(g1,g2)
    c: PointOnObject(g1,g2)
    c: Coincident(g3,g-3)
    c: Coincident(g4,g3)
    c: Coincident(g5,g3)
    c: Coincident(g5,g3)
    c: Vertical(g5)
    c: PointOnObject(g3,g5)
    c: PointOnObject(g4,g5)
    c: PointOnObject(g4,g5)
    c: Coincident(g6,g3)
    c: Coincident(g6,g0)
    c: Coincident(g7,g4)
    c: Coincident(g7,g1)
    c: Horizontal(g7)
    c: Coincident(g8,g4)
    c: Coincident(g8,g1)
    c: Coincident(g9,g3)
    c: Coincident(g9,g0)
    c: Horizontal(g9)
    c: Radius(g1) = 3.6
    c: Radius(g3) = 4
FEATURE [PartDesign::Pad] Pad002
  Length = 5
  Length2 = 100
  Profile = -> Sketch016
  Reversed = true
  Type = 0
FEATURE [Sketcher::SketchObject] Sketch017
  ExternalGeometry = -> [Pad002]
  MapMode = 5
  Placement = pos=(0,0,0) rot=(1,0,0;3.14159rad)
  Support = -> [Pad002]
  sketch-geometry (10):
    g0: ArcOfCircle CenterX=52.7584 CenterY=-58.25 CenterZ=0 NormalX=0 NormalY=0 NormalZ=1 Radius=4 StartAngle=1.5708 EndAngle=4.71239
    g1: ArcOfCircle CenterX=52.7584 CenterY=-58.25 CenterZ=0 NormalX=0 NormalY=0 NormalZ=1 Radius=3.6 StartAngle=1.5708 EndAngle=4.71239
    g2: ArcOfCircle CenterX=55.7584 CenterY=-58.25 CenterZ=0 NormalX=0 NormalY=0 NormalZ=1 Radius=3.6 StartAngle=4.71239 EndAngle=7.85398
    g3: ArcOfCircle CenterX=55.7584 CenterY=-58.25 CenterZ=0 NormalX=0 NormalY=0 NormalZ=1 Radius=4 StartAngle=4.71239 EndAngle=7.85398
    g4: LineSegment [constr] StartX=52.7584 StartY=-54.25 StartZ=0 EndX=52.7584 EndY=-62.25 EndZ=0
    g5: LineSegment [constr] StartX=55.7584 StartY=-54.25 StartZ=0 EndX=55.7584 EndY=-62.25 EndZ=0
    g6: LineSegment StartX=52.7584 StartY=-54.25 StartZ=0 EndX=55.7584 EndY=-54.25 EndZ=0
    g7: LineSegment StartX=52.7584 StartY=-54.65 StartZ=0 EndX=55.7584 EndY=-54.65 EndZ=0
    g8: LineSegment StartX=52.7584 StartY=-61.85 StartZ=0 EndX=55.7584 EndY=-61.85 EndZ=0
    g9: LineSegment StartX=52.7584 StartY=-62.25 StartZ=0 EndX=55.7584 EndY=-62.25 EndZ=0
  constraints (28):
    c: Coincident(g0,g-3)
    c: Coincident(g1,g0)
    c: Coincident(g2,g-4)
    c: Coincident(g3,g2)
    c: Coincident(g4,g0)
    c: Coincident(g4,g0)
    c: PointOnObject(g0,g4)
    c: Vertical(g4)
    c: PointOnObject(g1,g4)
    c: PointOnObject(g1,g4)
    c: Coincident(g5,g3)
    c: Coincident(g5,g3)
    c: PointOnObject(g2,g5)
    c: PointOnObject(g2,g5)
    c: PointOnObject(g2,g5)
    c: Vertical(g5)
    c: Coincident(g6,g0)
    c: Coincident(g6,g3)
    c: Horizontal(g6)
    c: Coincident(g7,g1)
    c: Coincident(g7,g2)
    c: Horizontal(g7)
    c: Coincident(g8,g1)
    c: Coincident(g8,g2)
    c: Coincident(g9,g0)
    c: Coincident(g9,g3)
    c: Radius(g1) = 3.6
    c: Radius(g3) = 4
FEATURE [PartDesign::Pad] Pad003
  Length = 5
  Length2 = 100
  Profile = -> Sketch017
  Reversed = true
  Type = 0
FEATURE [Sketcher::SketchObject] Sketch018
  ExternalGeometry = -> [Pad003]
  MapMode = 5
  Placement = pos=(0,0,0) rot=(1,0,0;3.14159rad)
  Support = -> [Pad003]
  sketch-geometry (10):
    g0: ArcOfCircle CenterX=38 CenterY=-17.75 CenterZ=0 NormalX=0 NormalY=0 NormalZ=1 Radius=4 StartAngle=1.5708 EndAngle=4.71239
    g1: ArcOfCircle CenterX=41 CenterY=-17.75 CenterZ=0 NormalX=0 NormalY=0 NormalZ=1 Radius=4 StartAngle=4.71239 EndAngle=7.85398
    g2: ArcOfCircle CenterX=38 CenterY=-17.75 CenterZ=0 NormalX=0 NormalY=0 NormalZ=1 Radius=3.6 StartAngle=1.5708 EndAngle=4.71239
    g3: ArcOfCircle CenterX=41 CenterY=-17.75 CenterZ=0 NormalX=0 NormalY=0 NormalZ=1 Radius=3.6 StartAngle=4.71239 EndAngle=7.85398
    g4: LineSegment [constr] StartX=38 StartY=-13.75 StartZ=0 EndX=38 EndY=-21.75 EndZ=0
    g5: LineSegment [constr] StartX=41 StartY=-13.75 StartZ=0 EndX=41 EndY=-21.75 EndZ=0
    g6: LineSegment StartX=38 StartY=-13.75 StartZ=0 EndX=41 EndY=-13.75 EndZ=0
    g7: LineSegment StartX=38 StartY=-14.15 StartZ=0 EndX=41 EndY=-14.15 EndZ=0
    g8: LineSegment StartX=38 StartY=-21.35 StartZ=0 EndX=41 EndY=-21.35 EndZ=0
    g9: LineSegment StartX=38 StartY=-21.75 StartZ=0 EndX=41 EndY=-21.75 EndZ=0
  constraints (28):
    c: Coincident(g0,g-4)
    c: Coincident(g1,g-3)
    c: Coincident(g2,g0)
    c: Coincident(g3,g1)
    c: Coincident(g4,g0)
    c: Coincident(g4,g0)
    c: PointOnObject(g0,g4)
    c: PointOnObject(g2,g4)
    c: PointOnObject(g2,g4)
    c: Coincident(g5,g1)
    c: Coincident(g5,g1)
    c: PointOnObject(g1,g5)
    c: PointOnObject(g3,g5)
    c: PointOnObject(g3,g5)
    c: Coincident(g6,g0)
    c: Coincident(g6,g1)
    c: Horizontal(g6)
    c: Coincident(g7,g2)
    c: Coincident(g7,g3)
    c: Horizontal(g7)
    c: Coincident(g8,g2)
    c: Coincident(g8,g3)
    c: Coincident(g9,g0)
    c: Coincident(g9,g1)
    c: Vertical(g4)
    c: Vertical(g5)
    c: Radius(g3) = 3.6
    c: Radius(g0) = 4
FEATURE [PartDesign::Pad] Pad004
  Length = 5
  Length2 = 100
  Profile = -> Sketch018
  Reversed = true
  Type = 0
FEATURE [Sketcher::SketchObject] Sketch019
  MapMode = 5
  Placement = pos=(-6.5,0,0) rot=(0.57735,-0.57735,-0.57735;2.0944rad)
  Support = -> [Pad004]
  sketch-geometry (5):
    g0: LineSegment StartX=-0.75 StartY=0 StartZ=0 EndX=0 EndY=0 EndZ=0
    g1: LineSegment StartX=0 StartY=0 StartZ=0 EndX=0 EndY=0.893816 EndZ=0
    g2: LineSegment [constr] StartX=0 StartY=0.893816 StartZ=0 EndX=-0.75 EndY=0.893816 EndZ=0
    g3: LineSegment [constr] StartX=-0.75 StartY=0.893816 StartZ=0 EndX=-0.75 EndY=0 EndZ=0
    g4: LineSegment StartX=-0.75 StartY=0 StartZ=0 EndX=0 EndY=0.893816 EndZ=0
  constraints (13):
    c: Coincident(g0,g1)
    c: Coincident(g1,g2)
    c: Coincident(g2,g3)
    c: Coincident(g3,g0)
    c: Horizontal(g0)
    c: Horizontal(g2)
    c: Vertical(g1)
    c: Vertical(g3)
    c: Coincident(g4,g0)
    c: Coincident(g4,g1)
    c: Angle(g0,g4) = 0.872665
    c: DistanceX(g0) = 0.75
    c: Coincident(g0,g-1)
FEATURE [PartDesign::Pocket] Pocket013
  Length = 5
  Midplane = true
  Profile = -> Sketch019
  Type = 1
FEATURE [Sketcher::SketchObject] Sketch020
  ExternalGeometry = -> [Pocket013]
  MapMode = 5
  Placement = pos=(0,0,28) rot=(0,0,1;0rad)
  Support = -> [Pocket013]
  sketch-geometry (6):
    g0: LineSegment StartX=13.9 StartY=62 StartZ=0 EndX=10.2 EndY=62 EndZ=0
    g1: LineSegment StartX=10.2 StartY=62 StartZ=0 EndX=10.2 EndY=50.625 EndZ=0
    g2: LineSegment [constr] StartX=10.2 StartY=50.625 StartZ=0 EndX=13.9 EndY=50.625 EndZ=0
    g3: LineSegment [constr] StartX=13.9 StartY=50.625 StartZ=0 EndX=13.9 EndY=62 EndZ=0
    g4: LineSegment StartX=10.2 StartY=50.625 StartZ=0 EndX=13.9 EndY=57.0336 EndZ=0
    g5: LineSegment StartX=13.9 StartY=57.0336 StartZ=0 EndX=13.9 EndY=62 EndZ=0
  constraints (15):
    c: Coincident(g0,g1)
    c: Coincident(g1,g2)
    c: Coincident(g3,g0)
    c: Horizontal(g0)
    c: Horizontal(g2)
    c: Vertical(g1)
    c: Vertical(g3)
    c: Coincident(g1,g-4)
    c: Coincident(g0,g-3)
    c: DistanceX(g0,g0) = -3.7
    c: Coincident(g4,g1)
    c: PointOnObject(g4,g3)
    c: Angle(g2,g4) = 1.0472
    c: Coincident(g5,g4)
    c: Coincident(g5,g0)
FEATURE [PartDesign::Pocket] Pocket014
  Length = 24
  Profile = -> Sketch020
  Type = 0
FEATURE [Sketcher::SketchObject] Sketch021
  ExternalGeometry = -> [Pocket014]
  MapMode = 5
  Placement = pos=(0,0,5.5) rot=(0,0,1;0rad)
  Support = -> [Pocket014]
  sketch-geometry (4):
    g0: LineSegment StartX=-6.5 StartY=50.625 StartZ=0 EndX=10.2 EndY=50.625 EndZ=0
    g1: LineSegment StartX=10.2 StartY=50.625 StartZ=0 EndX=10.2 EndY=62 EndZ=0
    g2: LineSegment StartX=10.2 StartY=62 StartZ=0 EndX=-6.5 EndY=62 EndZ=0
    g3: LineSegment StartX=-6.5 StartY=62 StartZ=0 EndX=-6.5 EndY=50.625 EndZ=0
  constraints (11):
    c: Coincident(g0,g1)
    c: Coincident(g1,g2)
    c: Coincident(g2,g3)
    c: Coincident(g3,g0)
    c: Horizontal(g0)
    c: Horizontal(g2)
    c: Vertical(g1)
    c: Vertical(g3)
    c: Coincident(g0,g-4)
    c: PointOnObject(g1,g-3)
    c: Coincident(g1,g-5)
FEATURE [PartDesign::Pocket] Pocket015
  Length = 1.5
  Profile = -> Sketch021
  Type = 0
FEATURE [Sketcher::SketchObject] Sketch022
  ExternalGeometry = -> [Pocket015]
  MapMode = 5
  Placement = pos=(-14.2713,8.2395,0) rot=(-0.377965,0.654654,0.654654;3.86433rad)
  Support = -> [Pocket015]
  sketch-geometry (21):
    g0: LineSegment StartX=-53.9702 StartY=24.2 StartZ=0 EndX=-51.3149 EndY=24.2 EndZ=0
    g1: LineSegment [constr] StartX=-51.3149 StartY=24.2 StartZ=0 EndX=-51.3149 EndY=19.8 EndZ=0
    g2: LineSegment StartX=-51.3149 StartY=19.8 StartZ=0 EndX=-53.9702 EndY=19.8 EndZ=0
    g3: LineSegment [constr] StartX=-53.9702 StartY=19.8 StartZ=0 EndX=-53.9702 EndY=24.2 EndZ=0
    g4: LineSegment StartX=-53.9702 StartY=8.4 StartZ=0 EndX=-51.3149 EndY=8.4 EndZ=0
    g5: LineSegment [constr] StartX=-51.3149 StartY=8.4 StartZ=0 EndX=-51.3149 EndY=4 EndZ=0
    g6: LineSegment StartX=-51.3149 StartY=4 StartZ=0 EndX=-53.9702 EndY=4 EndZ=0
    g7: LineSegment [constr] StartX=-53.9702 StartY=4 StartZ=0 EndX=-53.9702 EndY=8.4 EndZ=0
    g8: LineSegment StartX=-53.9702 StartY=8.4 StartZ=0 EndX=-55.2404 EndY=6.2 EndZ=0
    g9: LineSegment StartX=-55.2404 StartY=6.2 StartZ=0 EndX=-53.9702 EndY=4 EndZ=0
    g10: LineSegment StartX=-51.3149 StartY=8.4 StartZ=0 EndX=-50.0447 EndY=6.2 EndZ=0
    g11: LineSegment StartX=-50.0447 StartY=6.2 StartZ=0 EndX=-51.3149 EndY=4 EndZ=0
    g12: LineSegment [constr] StartX=-55.2404 StartY=6.2 StartZ=0 EndX=-50.0447 EndY=6.2 EndZ=0
    g13: LineSegment StartX=-53.9702 StartY=24.2 StartZ=0 EndX=-55.2404 EndY=22 EndZ=0
    g14: LineSegment StartX=-55.2404 StartY=22 StartZ=0 EndX=-53.9702 EndY=19.8 EndZ=0
    g15: LineSegment StartX=-51.3149 StartY=24.2 StartZ=0 EndX=-50.0447 EndY=22 EndZ=0
    g16: LineSegment StartX=-51.3149 StartY=19.8 StartZ=0 EndX=-50.0447 EndY=22 EndZ=0
    g17: LineSegment [constr] StartX=-55.2404 StartY=22 StartZ=0 EndX=-50.0447 EndY=22 EndZ=0
    g18: LineSegment [constr] StartX=-56.898 StartY=22 StartZ=0 EndX=-55.2404 EndY=22 EndZ=0
    g19: LineSegment [constr] StartX=-56.898 StartY=6.2 StartZ=0 EndX=-55.2404 EndY=6.2 EndZ=0
    g20: LineSegment [constr] StartX=-52.6425 StartY=24.2 StartZ=0 EndX=-52.6425 EndY=19.8 EndZ=0
  constraints (56):
    c: Coincident(g0,g1)
    c: Coincident(g1,g2)
    c: Coincident(g2,g3)
    c: Coincident(g3,g0)
    c: Horizontal(g0)
    c: Horizontal(g2)
    c: Vertical(g1)
    c: Vertical(g3)
    c: Coincident(g4,g5)
    c: Coincident(g5,g6)
    c: Coincident(g6,g7)
    c: Coincident(g7,g4)
    c: Horizontal(g4)
    c: Horizontal(g6)
    c: Vertical(g5)
    c: Vertical(g7)
    c: Coincident(g9,g8)
    c: Coincident(g9,g6)
    c: Coincident(g10,g4)
    c: Coincident(g11,g10)
    c: Coincident(g11,g5)
    c: Coincident(g8,g4)
    c: Coincident(g12,g8)
    c: Coincident(g12,g10)
    c: Horizontal(g12)
    c: Symmetric(g4,g6,g12)
    c: Coincident(g13,g0)
    c: Coincident(g14,g13)
    c: Coincident(g14,g2)
    c: Coincident(g15,g0)
    c: Coincident(g16,g1)
    c: Coincident(g16,g15)
    c: Coincident(g17,g13)
    c: Coincident(g17,g15)
    c: Horizontal(g17)
    c: Symmetric(g2,g0,g17)
    c: Parallel(g15,g14)
    c: Parallel(g8,g11)
    c: Parallel(g8,g13)
    c: PointOnObject(g1,g5)
    c: PointOnObject(g2,g7)
    c: Distance(g1) = 4.4
    c: DistanceY(g5) = -4.4
    c: Distance(g10,g4) = 4.5
    c: Angle(g9,g8) = 2.0944
    c: Coincident(g18,g-3)
    c: Coincident(g18,g13)
    c: Horizontal(g18)
    c: Coincident(g19,g-4)
    c: Coincident(g19,g8)
    c: Horizontal(g19)
    c: PointOnObject(g20,g0)
    c: PointOnObject(g20,g2)
    c: Vertical(g20)
    c: Symmetric(g0,g0,g20)
    c: Distance(g-5,g20) = 3.7
FEATURE [PartDesign::Pocket] Pocket016
  Length = 11
  Profile = -> Sketch022
  Type = 0
FEATURE [Sketcher::SketchObject] Sketch023
  ExternalGeometry = -> [Pocket016]
  MapMode = 5
  Placement = pos=(0,0,28) rot=(0,0,1;0rad)
  Support = -> [Pocket016]
  sketch-geometry (6):
    g0: LineSegment [constr] StartX=13.9 StartY=55.8212 StartZ=0 EndX=13.9 EndY=62 EndZ=0
    g1: LineSegment StartX=13.9 StartY=62 StartZ=0 EndX=5.5 EndY=62 EndZ=0
    g2: LineSegment StartX=5.5 StartY=62 StartZ=0 EndX=5.5 EndY=50.625 EndZ=0
    g3: LineSegment StartX=10.9 StartY=50.625 StartZ=0 EndX=13.9 EndY=55.8212 EndZ=0
    g4: LineSegment StartX=13.9 StartY=55.8212 StartZ=0 EndX=13.9 EndY=62 EndZ=0
    g5: LineSegment StartX=5.5 StartY=50.625 StartZ=0 EndX=10.9 EndY=50.625 EndZ=0
  constraints (16):
    c: Coincident(g0,g1)
    c: Coincident(g1,g2)
    c: Horizontal(g1)
    c: Vertical(g0)
    c: Vertical(g2)
    c: Coincident(g0,g-3)
    c: PointOnObject(g3,g0)
    c: Coincident(g4,g0)
    c: Coincident(g4,g3)
    c: DistanceX(g3,g0) = 3
    c: Coincident(g5,g2)
    c: Coincident(g3,g5)
    c: Horizontal(g5)
    c: Coincident(g2,g-4)
    c: Angle(g3,g5) = 2.0944
    c: Coincident(g0,g3)
FEATURE [PartDesign::Pad] Pad005
  Length = 24
  Length2 = 100
  Profile = -> Sketch023
  Reversed = true
  Type = 0
FEATURE [Sketcher::SketchObject] Sketch024
  ExternalGeometry = -> [Pad005]
  MapMode = 5
  Placement = pos=(-13.7463,7.93641,0) rot=(0.774597,0.447214,0.447214;1.82348rad)
  Support = -> [Pad005]
  sketch-geometry (6):
    g0: LineSegment StartX=50.0447 StartY=22 StartZ=0 EndX=51.3148 EndY=24.2 EndZ=0
    g1: LineSegment StartX=51.3148 StartY=24.2 StartZ=0 EndX=53.9702 EndY=24.2 EndZ=0
    g2: LineSegment StartX=53.9702 StartY=24.2 StartZ=0 EndX=55.2404 EndY=22 EndZ=0
    g3: LineSegment StartX=55.2404 StartY=22 StartZ=0 EndX=53.9702 EndY=19.8 EndZ=0
    g4: LineSegment StartX=53.9702 StartY=19.8 StartZ=0 EndX=51.3148 EndY=19.8 EndZ=0
    g5: LineSegment StartX=51.3148 StartY=19.8 StartZ=0 EndX=50.0447 EndY=22 EndZ=0
  constraints (14):
    c: Coincident(g-4,g0)
    c: Coincident(g0,g1)
    c: Horizontal(g1)
    c: Coincident(g1,g2)
    c: Coincident(g2,g-3)
    c: Coincident(g2,g3)
    c: Coincident(g3,g4)
    c: Horizontal(g4)
    c: Coincident(g4,g5)
    c: Coincident(g5,g0)
    c: Coincident(g0,g-4)
    c: Coincident(g1,g-3)
    c: Coincident(g4,g-5)
    c: Coincident(g3,g-5)
FEATURE [PartDesign::Pocket] Pocket017
  Length = 13
  Profile = -> Sketch024
  Type = 0
FEATURE [Sketcher::SketchObject] Sketch025
  ExternalGeometry = -> [Pocket017]
  MapMode = 5
  Placement = pos=(-13.7463,7.93641,0) rot=(0.774597,0.447214,0.447214;1.82348rad)
  Support = -> [Pocket017]
  sketch-geometry (11):
    g0: LineSegment [constr] StartX=51.3148 StartY=19.8 StartZ=0 EndX=51.3148 EndY=8.4 EndZ=0
    g1: LineSegment [constr] StartX=53.9702 StartY=19.8 StartZ=0 EndX=53.9702 EndY=8.4 EndZ=0
    g2: LineSegment StartX=51.3148 StartY=8.4 StartZ=0 EndX=53.9702 EndY=8.4 EndZ=0
    g3: LineSegment StartX=53.9702 StartY=8.4 StartZ=0 EndX=55.2404 EndY=6.2 EndZ=0
    g4: LineSegment StartX=55.2404 StartY=6.2 StartZ=0 EndX=53.9702 EndY=4 EndZ=0
    g5: LineSegment StartX=53.9702 StartY=4 StartZ=0 EndX=51.3148 EndY=4 EndZ=0
    g6: LineSegment StartX=51.3148 StartY=4 StartZ=0 EndX=50.0447 EndY=6.2 EndZ=0
    g7: LineSegment StartX=50.0447 StartY=6.2 StartZ=0 EndX=51.3148 EndY=8.4 EndZ=0
    g8: LineSegment [constr] StartX=50.0447 StartY=6.2 StartZ=0 EndX=55.2404 EndY=6.2 EndZ=0
    g9: LineSegment [constr] StartX=51.3148 StartY=8.4 StartZ=0 EndX=51.3148 EndY=4 EndZ=0
    g10: LineSegment [constr] StartX=53.9702 StartY=8.4 StartZ=0 EndX=53.9702 EndY=4 EndZ=0
  constraints (28):
    c: Coincident(g0,g-5)
    c: Vertical(g0)
    c: Coincident(g1,g-5)
    c: Vertical(g1)
    c: Coincident(g0,g2)
    c: Coincident(g2,g1)
    c: Horizontal(g2)
    c: Coincident(g2,g3)
    c: Coincident(g3,g4)
    c: Coincident(g4,g5)
    c: Horizontal(g5)
    c: Coincident(g5,g6)
    c: Coincident(g6,g7)
    c: Coincident(g7,g0)
    c: Coincident(g8,g6)
    c: Coincident(g8,g3)
    c: Horizontal(g8)
    c: Coincident(g9,g0)
    c: Coincident(g9,g5)
    c: Vertical(g9)
    c: Coincident(g10,g1)
    c: Coincident(g10,g4)
    c: Vertical(g10)
    c: Symmetric(g5,g0,g8)
    c: Parallel(g7,g-3)
    c: Parallel(g3,g-4)
    c: DistanceY(g10) = -4.4
    c: DistanceY(g1) = -11.4
FEATURE [PartDesign::Pocket] Pocket018
  Length = 10
  Profile = -> Sketch025
  Type = 0
FEATURE [Sketcher::SketchObject] Sketch026
  ExternalGeometry = -> [Pocket018]
  MapMode = 5
  Placement = pos=(5.5,0,0) rot=(0.57735,-0.57735,-0.57735;2.0944rad)
  Support = -> [Pocket018]
  sketch-geometry (9):
    g0: LineSegment StartX=-54.4355 StartY=8.4 StartZ=0 EndX=-52.0917 EndY=8.4 EndZ=0
    g1: LineSegment StartX=-52.0917 StartY=8.4 StartZ=0 EndX=-50.625 EndY=6.2 EndZ=0
    g2: LineSegment StartX=-50.625 StartY=6.2 StartZ=0 EndX=-52.0917 EndY=4 EndZ=0
    g3: LineSegment StartX=-52.0917 StartY=4 StartZ=0 EndX=-54.4355 EndY=4 EndZ=0
    g4: LineSegment StartX=-54.4355 StartY=4 StartZ=0 EndX=-55.9022 EndY=6.2 EndZ=0
    g5: LineSegment StartX=-55.9022 StartY=6.2 StartZ=0 EndX=-54.4355 EndY=8.4 EndZ=0
    g6: LineSegment [constr] StartX=-55.9022 StartY=6.2 StartZ=0 EndX=-50.625 EndY=6.2 EndZ=0
    g7: LineSegment [constr] StartX=-52.0917 StartY=8.4 StartZ=0 EndX=-52.0917 EndY=4 EndZ=0
    g8: LineSegment [constr] StartX=-54.4355 StartY=4 StartZ=0 EndX=-54.4355 EndY=8.4 EndZ=0
  constraints (24):
    c: Horizontal(g0)
    c: Coincident(g0,g1)
    c: Coincident(g1,g2)
    c: Coincident(g2,g3)
    c: Horizontal(g3)
    c: Coincident(g3,g4)
    c: Coincident(g4,g5)
    c: Coincident(g5,g0)
    c: Coincident(g6,g4)
    c: Coincident(g6,g1)
    c: Horizontal(g6)
    c: Coincident(g7,g0)
    c: Coincident(g7,g2)
    c: Vertical(g7)
    c: Symmetric(g2,g0,g6)
    c: PointOnObject(g-3,g0)
    c: PointOnObject(g-4,g3)
    c: Parallel(g1,g-3)
    c: Parallel(g5,g-4)
    c: Coincident(g8,g3)
    c: Coincident(g8,g0)
    c: Vertical(g8)
    c: Distance(g4,g2) = 4.4
    c: PointOnObject(g1,g-5)
FEATURE [PartDesign::Pocket] Pocket019
  Length = 18
  Profile = -> Sketch026
  Type = 0
FEATURE [Sketcher::SketchObject] Sketch027
  ExternalGeometry = -> [Pocket019]
  MapMode = 5
  Placement = pos=(5.5,0,0) rot=(0.57735,-0.57735,-0.57735;2.0944rad)
  Support = -> [Pocket019]
  sketch-geometry (9):
    g0: LineSegment StartX=-55.9022 StartY=22 StartZ=0 EndX=-54.4355 EndY=24.2 EndZ=0
    g1: LineSegment StartX=-54.4355 StartY=24.2 StartZ=0 EndX=-52.0917 EndY=24.2 EndZ=0
    g2: LineSegment StartX=-52.0917 StartY=24.2 StartZ=0 EndX=-50.625 EndY=22 EndZ=0
    g3: LineSegment StartX=-50.625 StartY=22 StartZ=0 EndX=-52.0917 EndY=19.8 EndZ=0
    g4: LineSegment StartX=-52.0917 StartY=19.8 StartZ=0 EndX=-54.4355 EndY=19.8 EndZ=0
    g5: LineSegment StartX=-54.4355 StartY=19.8 StartZ=0 EndX=-55.9022 EndY=22 EndZ=0
    g6: LineSegment [constr] StartX=-55.9022 StartY=22 StartZ=0 EndX=-50.625 EndY=22 EndZ=0
    g7: LineSegment [constr] StartX=-54.4355 StartY=24.2 StartZ=0 EndX=-54.4355 EndY=19.8 EndZ=0
    g8: LineSegment [constr] StartX=-52.0917 StartY=24.2 StartZ=0 EndX=-52.0917 EndY=19.8 EndZ=0
  constraints (24):
    c: Coincident(g0,g1)
    c: Horizontal(g1)
    c: Coincident(g1,g2)
    c: Coincident(g2,g3)
    c: Coincident(g3,g4)
    c: Horizontal(g4)
    c: Coincident(g4,g5)
    c: Coincident(g5,g0)
    c: Coincident(g6,g0)
    c: Coincident(g6,g2)
    c: Horizontal(g6)
    c: Coincident(g7,g0)
    c: Coincident(g7,g4)
    c: Vertical(g7)
    c: Coincident(g8,g1)
    c: Coincident(g8,g3)
    c: Vertical(g8)
    c: Symmetric(g4,g0,g6)
    c: Parallel(g-3,g2)
    c: Parallel(g5,g-3)
    c: PointOnObject(g-3,g1)
    c: PointOnObject(g-4,g4)
    c: Distance(g0,g2) = 4.4
    c: PointOnObject(g2,g-5)
FEATURE [PartDesign::Pocket] Pocket020
  Length = 18
  Profile = -> Sketch027
  Type = 0
FEATURE [Sketcher::SketchObject] Sketch028
  ExternalGeometry = -> [Pocket020]
  MapMode = 5
  Placement = pos=(5.5,0,0) rot=(0.57735,-0.57735,-0.57735;2.0944rad)
  Support = -> [Pocket020]
  sketch-geometry (4):
    g0: LineSegment StartX=-56.0779 StartY=24.2 StartZ=0 EndX=-54.4355 EndY=24.2 EndZ=0
    g1: LineSegment StartX=-54.4355 StartY=24.2 StartZ=0 EndX=-54.4355 EndY=19.8 EndZ=0
    g2: LineSegment StartX=-54.4355 StartY=19.8 StartZ=0 EndX=-56.0779 EndY=19.8 EndZ=0
    g3: LineSegment StartX=-56.0779 StartY=19.8 StartZ=0 EndX=-56.0779 EndY=24.2 EndZ=0
  constraints (10):
    c: Coincident(g0,g1)
    c: Coincident(g1,g2)
    c: Coincident(g2,g3)
    c: Coincident(g3,g0)
    c: Horizontal(g0)
    c: Horizontal(g2)
    c: Vertical(g1)
    c: Vertical(g3)
    c: Coincident(g0,g-3)
    c: Coincident(g-4,g2)
FEATURE [PartDesign::Pocket] Pocket021
  Length = 5
  Profile = -> Sketch028
  Type = 0
FEATURE [Sketcher::SketchObject] Sketch029
  ExternalGeometry = -> [Pocket021]
  MapMode = 5
  Placement = pos=(5.5,0,0) rot=(0.57735,-0.57735,-0.57735;2.0944rad)
  Support = -> [Pocket021]
  sketch-geometry (4):
    g0: LineSegment StartX=-56.0779 StartY=8.4 StartZ=0 EndX=-54.4355 EndY=8.4 EndZ=0
    g1: LineSegment StartX=-54.4355 StartY=8.4 StartZ=0 EndX=-54.4355 EndY=4 EndZ=0
    g2: LineSegment StartX=-54.4355 StartY=4 StartZ=0 EndX=-56.0779 EndY=4 EndZ=0
    g3: LineSegment StartX=-56.0779 StartY=4 StartZ=0 EndX=-56.0779 EndY=8.4 EndZ=0
  constraints (10):
    c: Coincident(g0,g1)
    c: Coincident(g1,g2)
    c: Coincident(g2,g3)
    c: Coincident(g3,g0)
    c: Horizontal(g0)
    c: Horizontal(g2)
    c: Vertical(g1)
    c: Vertical(g3)
    c: Coincident(g0,g-4)
    c: Coincident(g1,g-3)
FEATURE [PartDesign::Pocket] Pocket022
  Length = 5
  Profile = -> Sketch029
  Type = 0
FEATURE [Sketcher::SketchObject] Sketch030
  ExternalGeometry = -> [Pocket022]
  MapMode = 5
  Placement = pos=(15.7,0,0) rot=(0.57735,-0.57735,-0.57735;2.0944rad)
  Support = -> [Pocket022]
  sketch-geometry (4):
    g0: LineSegment StartX=-52.0917 StartY=4 StartZ=0 EndX=-49.4791 EndY=4 EndZ=0
    g1: LineSegment StartX=-49.4791 StartY=4 StartZ=0 EndX=-49.4791 EndY=8.4 EndZ=0
    g2: LineSegment StartX=-49.4791 StartY=8.4 StartZ=0 EndX=-52.0917 EndY=8.4 EndZ=0
    g3: LineSegment StartX=-52.0917 StartY=8.4 StartZ=0 EndX=-52.0917 EndY=4 EndZ=0
  constraints (11):
    c: Coincident(g0,g1)
    c: Coincident(g1,g2)
    c: Coincident(g2,g3)
    c: Coincident(g3,g0)
    c: Horizontal(g0)
    c: Horizontal(g2)
    c: Vertical(g1)
    c: Vertical(g3)
    c: PointOnObject(g1,g-4)
    c: Coincident(g-5,g0)
    c: Coincident(g0,g-3)
FEATURE [PartDesign::Pocket] Pocket023
  Length = 7.8
  Profile = -> Sketch030
  Type = 0
FEATURE [Sketcher::SketchObject] Sketch031
  ExternalGeometry = -> [Pocket023]
  MapMode = 5
  Placement = pos=(0,62,0) rot=(0,0.707107,0.707107;3.14159rad)
  Support = -> [Pocket023]
  sketch-geometry (7):
    g0: LineSegment [constr] StartX=-13.9 StartY=25 StartZ=0 EndX=-10.2 EndY=25 EndZ=0
    g1: LineSegment StartX=-10.2 StartY=25 StartZ=0 EndX=-10.2 EndY=18.3 EndZ=0
    g2: LineSegment StartX=-10.2 StartY=18.3 StartZ=0 EndX=-13.9 EndY=18.3 EndZ=0
    g3: LineSegment StartX=-13.9 StartY=18.3 StartZ=0 EndX=-13.9 EndY=25 EndZ=0
    g4: LineSegment StartX=-13.9 StartY=25 StartZ=0 EndX=-13.1448 EndY=25.9 EndZ=0
    g5: LineSegment StartX=-13.1448 StartY=25.9 StartZ=0 EndX=-10.9552 EndY=25.9 EndZ=0
    g6: LineSegment StartX=-10.9552 StartY=25.9 StartZ=0 EndX=-10.2 EndY=25 EndZ=0
  constraints (20):
    c: Coincident(g0,g1)
    c: Coincident(g1,g2)
    c: Coincident(g2,g3)
    c: Coincident(g3,g0)
    c: Horizontal(g0)
    c: Horizontal(g2)
    c: Vertical(g1)
    c: Vertical(g3)
    c: Coincident(g4,g0)
    c: Coincident(g5,g4)
    c: Horizontal(g5)
    c: Coincident(g6,g0)
    c: Angle(g6,g0) = 0.872665
    c: Angle(g0,g4) = 0.872665
    c: DistanceY(g0,g4) = 0.9
    c: Coincident(g5,g6)
    c: DistanceX(g2) = -3.7
    c: DistanceX(g0,g-3) = 4.7
    c: DistanceY(g3) = 6.7
    c: DistanceY(g4,g-3) = 2.1
FEATURE [PartDesign::Pocket] Pocket024
  Length = 11.8
  Profile = -> Sketch031
  Type = 0
FEATURE [Sketcher::SketchObject] Sketch032
  ExternalGeometry = -> [Pocket024]
  MapMode = 5
  Placement = pos=(0,62,0) rot=(0,0.707107,0.707107;3.14159rad)
  Support = -> [Pocket024]
  sketch-geometry (7):
    g0: LineSegment [constr] StartX=-13.9 StartY=9.2 StartZ=0 EndX=-10.2 EndY=9.2 EndZ=0
    g1: LineSegment StartX=-10.2 StartY=9.2 StartZ=0 EndX=-10.2 EndY=2.5 EndZ=0
    g2: LineSegment StartX=-10.2 StartY=2.5 StartZ=0 EndX=-13.9 EndY=2.5 EndZ=0
    g3: LineSegment StartX=-13.9 StartY=2.5 StartZ=0 EndX=-13.9 EndY=9.2 EndZ=0
    g4: LineSegment StartX=-13.1448 StartY=10.1 StartZ=0 EndX=-10.9552 EndY=10.1 EndZ=0
    g5: LineSegment StartX=-10.9552 StartY=10.1 StartZ=0 EndX=-10.2 EndY=9.2 EndZ=0
    g6: LineSegment StartX=-13.1448 StartY=10.1 StartZ=0 EndX=-13.9 EndY=9.2 EndZ=0
  constraints (20):
    c: Coincident(g0,g1)
    c: Coincident(g1,g2)
    c: Coincident(g2,g3)
    c: Coincident(g3,g0)
    c: Horizontal(g0)
    c: Horizontal(g2)
    c: Vertical(g1)
    c: Vertical(g3)
    c: PointOnObject(g-3,g1)
    c: PointOnObject(g-3,g3)
    c: Horizontal(g4)
    c: Coincident(g5,g4)
    c: Coincident(g5,g0)
    c: Coincident(g6,g4)
    c: Coincident(g6,g0)
    c: Angle(g0,g6) = 0.872665
    c: Angle(g5,g0) = 0.872665
    c: DistanceY(g4,g0) = -0.9
    c: DistanceY(g2,g0) = 6.7
    c: DistanceY(g-3,g4) = -8.2
FEATURE [PartDesign::Pocket] Pocket025
  Length = 11.8
  Profile = -> Sketch032
  Type = 0
FEATURE [Sketcher::SketchObject] Sketch033
  MapMode = 5
  Placement = pos=(0,2.5e-11,0) rot=(1,0,0;1.5708rad)
  Support = -> [Pocket025]
  sketch-geometry (6):
    g0: Circle [constr] CenterX=0 CenterY=14 CenterZ=0 NormalX=0 NormalY=0 NormalZ=1 Radius=2.05
    g1: LineSegment StartX=-1.57039 StartY=15.3177 StartZ=0 EndX=-0.578336 EndY=16.5 EndZ=0
    g2: LineSegment StartX=-0.578336 StartY=16.5 StartZ=0 EndX=0.578336 EndY=16.5 EndZ=0
    g3: LineSegment StartX=0.578336 StartY=16.5 StartZ=0 EndX=1.57039 EndY=15.3177 EndZ=0
    g4: LineSegment [constr] StartX=0 StartY=14 StartZ=0 EndX=0 EndY=16.5 EndZ=0
    g5: ArcOfCircle CenterX=0 CenterY=14 CenterZ=0 NormalX=0 NormalY=0 NormalZ=1 Radius=2.05 StartAngle=2.44346 EndAngle=6.98132
  constraints (18):
    c: Radius(g0) = 2.05
    c: DistanceY(g0) = 14
    c: PointOnObject(g1,g0)
    c: Tangent(g1,g0)
    c: Coincident(g2,g1)
    c: Horizontal(g2)
    c: Coincident(g3,g2)
    c: PointOnObject(g3,g0)
    c: Tangent(g3,g0)
    c: Coincident(g4,g0)
    c: PointOnObject(g4,g2)
    c: Symmetric(g2,g1,g4)
    c: DistanceY(g2,g0) = -2.5
    c: Angle(g2,g3) = 2.26893
    c: PointOnObject(g0,g-2)
    c: Coincident(g5,g0)
    c: Coincident(g5,g3)
    c: Coincident(g5,g1)
FEATURE [PartDesign::Pocket] Pocket026
  Length = 36
  Profile = -> Sketch033
  Type = 0
FEATURE [Sketcher::SketchObject] Sketch034
  ExternalGeometry = -> [Pocket026]
  MapMode = 5
  Placement = pos=(0,2.5e-11,0) rot=(1,0,0;1.5708rad)
  Support = -> [Pocket026]
  sketch-geometry (2):
    g0: Circle CenterX=-25 CenterY=14 CenterZ=0 NormalX=0 NormalY=0 NormalZ=1 Radius=2.35
    g1: LineSegment [constr] StartX=-25 StartY=14 StartZ=0 EndX=0 EndY=14 EndZ=0
  constraints (5):
    c: Radius(g0) = 2.35
    c: Coincident(g1,g-3)
    c: Horizontal(g1)
    c: DistanceX(g1) = 25
    c: Coincident(g0,g1)
FEATURE [PartDesign::Pocket] Pocket027
  Length = 9
  Profile = -> Sketch034
  Type = 0
FEATURE [Sketcher::SketchObject] Sketch035
  ExternalGeometry = -> [Pocket027]
  MapMode = 5
  Placement = pos=(0,2.5e-11,0) rot=(1,0,0;1.5708rad)
  Support = -> [Pocket027]
  sketch-geometry (2):
    g0: Circle CenterX=25 CenterY=14 CenterZ=0 NormalX=0 NormalY=0 NormalZ=1 Radius=2.35
    g1: LineSegment [constr] StartX=0 StartY=14 StartZ=0 EndX=25 EndY=14 EndZ=0
  constraints (5):
    c: Coincident(g1,g-3)
    c: Coincident(g1,g0)
    c: Horizontal(g1)
    c: Radius(g0) = 2.35
    c: DistanceX(g1) = 25
FEATURE [PartDesign::Pocket] Pocket028
  Length = 7
  Profile = -> Sketch035
  Type = 0
FEATURE [Sketcher::SketchObject] Sketch036
  ExternalGeometry = -> [Pocket028]
  MapMode = 5
  Placement = pos=(0,7,0) rot=(0,0.707107,0.707107;3.14159rad)
  Support = -> [Pocket028]
  sketch-geometry (13):
    g0: LineSegment [constr] StartX=-27.1016 StartY=17.64 StartZ=0 EndX=-22.8984 EndY=17.64 EndZ=0
    g1: LineSegment [constr] StartX=-22.8984 StartY=17.64 StartZ=0 EndX=-22.8984 EndY=10.36 EndZ=0
    g2: LineSegment StartX=-22.8984 StartY=10.36 StartZ=0 EndX=-27.1016 EndY=10.36 EndZ=0
    g3: LineSegment [constr] StartX=-27.1016 StartY=10.36 StartZ=0 EndX=-27.1016 EndY=17.64 EndZ=0
    g4: LineSegment StartX=-27.1016 StartY=17.64 StartZ=0 EndX=-29.2031 EndY=14 EndZ=0
    g5: LineSegment StartX=-29.2031 StartY=14 StartZ=0 EndX=-27.1016 EndY=10.36 EndZ=0
    g6: LineSegment StartX=-22.8984 StartY=17.64 StartZ=0 EndX=-20.7969 EndY=14 EndZ=0
    g7: LineSegment StartX=-20.7969 StartY=14 StartZ=0 EndX=-22.8984 EndY=10.36 EndZ=0
    g8: LineSegment [constr] StartX=-29.2031 StartY=14 StartZ=0 EndX=-20.7969 EndY=14 EndZ=0
    g9: LineSegment [constr] StartX=-25 StartY=14 StartZ=0 EndX=-25 EndY=17.64 EndZ=0
    g10: LineSegment StartX=-27.1016 StartY=17.64 StartZ=0 EndX=-26.8129 EndY=18.14 EndZ=0
    g11: LineSegment StartX=-26.8129 StartY=18.14 StartZ=0 EndX=-23.1871 EndY=18.14 EndZ=0
    g12: LineSegment StartX=-23.1871 StartY=18.14 StartZ=0 EndX=-22.8984 EndY=17.64 EndZ=0
  constraints (35):
    c: Coincident(g0,g1)
    c: Coincident(g1,g2)
    c: Coincident(g2,g3)
    c: Coincident(g3,g0)
    c: Horizontal(g0)
    c: Horizontal(g2)
    c: Vertical(g1)
    c: Vertical(g3)
    c: Coincident(g0,g4)
    c: Coincident(g4,g5)
    c: Coincident(g5,g2)
    c: Coincident(g0,g6)
    c: Coincident(g6,g7)
    c: Coincident(g7,g1)
    c: Coincident(g8,g4)
    c: Horizontal(g8)
    c: Coincident(g6,g8)
    c: Symmetric(g2,g0,g8)
    c: Angle(g5,g4) = 2.0944
    c: Angle(g6,g7) = 2.0944
    c: PointOnObject(g-3,g8)
    c: PointOnObject(g9,g0)
    c: Vertical(g9)
    c: Coincident(g9,g-3)
    c: DistanceY(g0,g2) = -7.28
    c: Distance(g4,g1) = 7.28
    c: Symmetric(g0,g0,g9)
    c: Coincident(g10,g0)
    c: Coincident(g11,g10)
    c: Horizontal(g11)
    c: Coincident(g12,g11)
    c: Coincident(g12,g0)
    c: Parallel(g12,g6)
    c: Parallel(g10,g4)
    c: DistanceY(g10,g0) = -0.5
FEATURE [PartDesign::Pocket] Pocket029
  Length = 3.5
  Profile = -> Sketch036
  Type = 0
FEATURE [Sketcher::SketchObject] Sketch037
  ExternalGeometry = -> [Pocket029]
  MapMode = 5
  Placement = pos=(0,7,0) rot=(0,0.707107,0.707107;3.14159rad)
  Support = -> [Pocket029]
  sketch-geometry (13):
    g0: LineSegment [constr] StartX=22.8984 StartY=17.64 StartZ=0 EndX=27.1016 EndY=17.64 EndZ=0
    g1: LineSegment [constr] StartX=27.1016 StartY=17.64 StartZ=0 EndX=27.1016 EndY=10.36 EndZ=0
    g2: LineSegment StartX=27.1016 StartY=10.36 StartZ=0 EndX=22.8984 EndY=10.36 EndZ=0
    g3: LineSegment [constr] StartX=22.8984 StartY=10.36 StartZ=0 EndX=22.8984 EndY=17.64 EndZ=0
    g4: LineSegment [constr] StartX=25 StartY=14 StartZ=0 EndX=25 EndY=17.64 EndZ=0
    g5: LineSegment StartX=22.8984 StartY=17.64 StartZ=0 EndX=20.7969 EndY=14 EndZ=0
    g6: LineSegment StartX=20.7969 StartY=14 StartZ=0 EndX=22.8984 EndY=10.36 EndZ=0
    g7: LineSegment StartX=27.1016 StartY=17.64 StartZ=0 EndX=29.2031 EndY=14 EndZ=0
    g8: LineSegment StartX=29.2031 StartY=14 StartZ=0 EndX=27.1016 EndY=10.36 EndZ=0
    g9: LineSegment [constr] StartX=20.7969 StartY=14 StartZ=0 EndX=29.2031 EndY=14 EndZ=0
    g10: LineSegment StartX=22.8984 StartY=17.64 StartZ=0 EndX=23.1871 EndY=18.14 EndZ=0
    g11: LineSegment StartX=27.1016 StartY=17.64 StartZ=0 EndX=26.8129 EndY=18.14 EndZ=0
    g12: LineSegment StartX=23.1871 StartY=18.14 StartZ=0 EndX=26.8129 EndY=18.14 EndZ=0
  constraints (35):
    c: Coincident(g0,g1)
    c: Coincident(g1,g2)
    c: Coincident(g2,g3)
    c: Coincident(g3,g0)
    c: Horizontal(g0)
    c: Horizontal(g2)
    c: Vertical(g1)
    c: Vertical(g3)
    c: Coincident(g4,g-3)
    c: PointOnObject(g4,g0)
    c: Vertical(g4)
    c: Symmetric(g0,g0,g4)
    c: Coincident(g0,g5)
    c: Coincident(g5,g6)
    c: Coincident(g6,g2)
    c: Coincident(g0,g7)
    c: Coincident(g7,g8)
    c: Coincident(g8,g1)
    c: Coincident(g9,g5)
    c: Coincident(g9,g7)
    c: Horizontal(g9)
    c: PointOnObject(g4,g9)
    c: Angle(g6,g5) = 2.0944
    c: Angle(g7,g8) = 2.0944
    c: DistanceY(g3) = 7.28
    c: Distance(g0,g7) = 7.28
    c: Parallel(g5,g8)
    c: Coincident(g10,g0)
    c: Coincident(g11,g0)
    c: Coincident(g12,g10)
    c: Coincident(g12,g11)
    c: Horizontal(g12)
    c: Parallel(g11,g7)
    c: Parallel(g10,g5)
    c: DistanceY(g10,g0) = -0.5
FEATURE [PartDesign::Pocket] Pocket030
  Length = 3.5
  Profile = -> Sketch037
  Type = 0
FEATURE [Sketcher::SketchObject] Sketch038
  ExternalGeometry = -> [Pocket030]
  MapMode = 5
  Placement = pos=(0,0,8) rot=(1,0,0;3.14159rad)
  Support = -> [Pocket030]
  sketch-geometry (2):
    g0: Circle CenterX=4.6 CenterY=-38 CenterZ=0 NormalX=0 NormalY=0 NormalZ=1 Radius=4.4
    g1: Circle CenterX=4.6 CenterY=-38 CenterZ=0 NormalX=0 NormalY=0 NormalZ=1 Radius=4
  constraints (4):
    c: Coincident(g0,g-3)
    c: Coincident(g1,g0)
    c: Equal(g-3,g1)
    c: Radius(g0) = 4.4
FEATURE [PartDesign::Pocket] Pocket031
  Length = 1
  Profile = -> Sketch038
  Type = 0
FEATURE [Sketcher::SketchObject] Sketch040
  ExternalGeometry = -> [Pocket031]
  MapMode = 5
  Placement = pos=(0,0,8.32) rot=(1,0,0;3.14159rad)
  Support = -> [Pocket031]
  sketch-geometry (4):
    g0: LineSegment StartX=-6.5 StartY=-13 StartZ=0 EndX=-18.5 EndY=-13 EndZ=0
    g1: LineSegment StartX=-18.5 StartY=-13 StartZ=0 EndX=-18.5 EndY=-27 EndZ=0
    g2: LineSegment StartX=-18.5 StartY=-27 StartZ=0 EndX=-6.5 EndY=-27 EndZ=0
    g3: LineSegment StartX=-6.5 StartY=-27 StartZ=0 EndX=-6.5 EndY=-13 EndZ=0
  constraints (11):
    c: Coincident(g0,g1)
    c: Coincident(g1,g2)
    c: Coincident(g2,g3)
    c: Coincident(g3,g0)
    c: Horizontal(g0)
    c: Horizontal(g2)
    c: Vertical(g1)
    c: Vertical(g3)
    c: Coincident(g0,g-3)
    c: Coincident(g2,g-3)
    c: DistanceX(g0) = -12
FEATURE [PartDesign::Pocket] Pocket032
  Length = 0.32
  Profile = -> Sketch040
  Type = 0
FEATURE [Part::Feature] Pocket032001  label="Pocket033"
  shape: bbox 97.06 x 64.55 x 28 mm, 171 faces (baked)
FEATURE [Sketcher::SketchObject] Sketch042
  ExternalGeometry = -> [Pocket032001]
  MapMode = 5
  Placement = pos=(0,0,8.64) rot=(1,0,0;3.14159rad)
  Support = -> [Pocket032001]
  sketch-geometry (2):
    g0: Circle CenterX=-12.5 CenterY=-21.75 CenterZ=0 NormalX=0 NormalY=0 NormalZ=1 Radius=2.35
    g1: Circle CenterX=-12.5 CenterY=-21.75 CenterZ=0 NormalX=0 NormalY=0 NormalZ=1 Radius=1.95
  constraints (4):
    c: Coincident(g0,g-3)
    c: Coincident(g1,g0)
    c: Radius(g1) = 1.95
    c: Radius(g0) = 2.35
FEATURE [PartDesign::Pad] Pad006
  Length = 8.6
  Length2 = 100
  Profile = -> Sketch042
  Type = 0
FEATURE [Sketcher::SketchObject] Sketch043
  ExternalGeometry = -> [Pad006]
  MapMode = 5
  Placement = pos=(0,0,8.64) rot=(1,0,0;3.14159rad)
  Support = -> [Pad006]
  sketch-geometry (11):
    g0: ArcOfCircle CenterX=-12.5 CenterY=-21.75 CenterZ=0 NormalX=0 NormalY=0 NormalZ=1 Radius=5.25 StartAngle=2.02287 EndAngle=4.71239
    g1: LineSegment StartX=-14.7934 StartY=-17.0274 StartZ=0 EndX=-7.67473 EndY=-13.5705 EndZ=0
    g2: LineSegment StartX=-12.5 StartY=-27 StartZ=0 EndX=-7.5 EndY=-27 EndZ=0
    g3: LineSegment StartX=-7.5 StartY=-27 StartZ=0 EndX=-7.5 EndY=-26.6 EndZ=0
    g4: LineSegment StartX=-7.5 StartY=-26.6 StartZ=0 EndX=-12.5 EndY=-26.6 EndZ=0
    g5: LineSegment [constr] StartX=-12.5 StartY=-26.6 StartZ=0 EndX=-12.5 EndY=-27 EndZ=0
    g6: ArcOfCircle CenterX=-12.5 CenterY=-21.75 CenterZ=0 NormalX=0 NormalY=0 NormalZ=1 Radius=4.85 StartAngle=2.02287 EndAngle=4.71239
    g7: LineSegment [constr] StartX=-14.7934 StartY=-17.0274 StartZ=0 EndX=-14.6186 EndY=-17.3872 EndZ=0
    g8: LineSegment StartX=-7.67473 StartY=-13.5705 StartZ=0 EndX=-7.5 EndY=-13.9303 EndZ=0
    g9: LineSegment StartX=-14.6186 StartY=-17.3872 StartZ=0 EndX=-7.5 EndY=-13.9303 EndZ=0
    g10: LineSegment [constr] StartX=-7.5 StartY=-26.6 StartZ=0 EndX=-7.5 EndY=-13.9303 EndZ=0
  constraints (31):
    c: Coincident(g0,g-3)
    c: Horizontal(g2)
    c: PointOnObject(g-4,g2)
    c: Coincident(g1,g0)
    c: PointOnObject(g-4,g1)
    c: Radius(g0) = 5.25
    c: Coincident(g2,g0)
    c: Coincident(g0,g-5)
    c: Coincident(g3,g2)
    c: Vertical(g3)
    c: Coincident(g4,g3)
    c: Horizontal(g4)
    c: Coincident(g5,g4)
    c: Vertical(g5)
    c: Coincident(g5,g0)
    c: DistanceY(g3) = 0.4
    c: DistanceX(g2,g-4) = 1
    c: Coincident(g6,g0)
    c: Coincident(g6,g4)
    c: Coincident(g7,g0)
    c: Coincident(g7,g6)
    c: Coincident(g8,g1)
    c: Perpendicular(g8,g1)
    c: Coincident(g9,g6)
    c: Coincident(g9,g8)
    c: Perpendicular(g9,g8)
    c: Distance(g8) = 0.4
    c: Perpendicular(g7,g9)
    c: Coincident(g10,g3)
    c: Vertical(g10)
    c: Coincident(g8,g10)
FEATURE [PartDesign::Pad] Pad007
  Length = 8.6
  Length2 = 100
  Profile = -> Sketch043
  Type = 0
FEATURE [Sketcher::SketchObject] Sketch044
  ExternalGeometry = -> [Pad007]
  MapMode = 5
  Placement = pos=(0,0,0.0399993) rot=(1,0,0;3.14159rad)
  Support = -> [Pad007]
  sketch-geometry (12):
    g0: LineSegment StartX=-8.41568 StartY=-27 StartZ=0 EndX=-7.5 EndY=-27 EndZ=0
    g1: LineSegment StartX=-7.5 StartY=-27 StartZ=0 EndX=-7.5 EndY=-13.9303 EndZ=0
    g2: LineSegment StartX=-7.5 StartY=-13.9303 StartZ=0 EndX=-8.41568 EndY=-13.9303 EndZ=0
    g3: LineSegment [constr] StartX=-8.41568 StartY=-13.9303 StartZ=0 EndX=-8.41568 EndY=-27 EndZ=0
    g4: LineSegment [constr] StartX=-7.5 StartY=-20.75 StartZ=0 EndX=-17.6539 EndY=-20.75 EndZ=0
    g5: LineSegment StartX=-17.6539 StartY=-20.75 StartZ=0 EndX=-17.6539 EndY=-22.75 EndZ=0
    g6: LineSegment [constr] StartX=-17.6539 StartY=-22.75 StartZ=0 EndX=-7.5 EndY=-22.75 EndZ=0
    g7: LineSegment StartX=-7.5 StartY=-22.75 StartZ=0 EndX=-7.5 EndY=-20.75 EndZ=0
    g8: LineSegment StartX=-17.6539 StartY=-20.75 StartZ=0 EndX=-8.41568 EndY=-20.75 EndZ=0
    g9: LineSegment StartX=-17.6539 StartY=-22.75 StartZ=0 EndX=-8.41568 EndY=-22.75 EndZ=0
    g10: LineSegment StartX=-8.41568 StartY=-20.75 StartZ=0 EndX=-8.41568 EndY=-13.9303 EndZ=0
    g11: LineSegment StartX=-8.41568 StartY=-22.75 StartZ=0 EndX=-8.41568 EndY=-27 EndZ=0
  constraints (33):
    c: Coincident(g0,g1)
    c: Coincident(g1,g2)
    c: Coincident(g2,g3)
    c: Coincident(g3,g0)
    c: Horizontal(g0)
    c: Horizontal(g2)
    c: Vertical(g1)
    c: Vertical(g3)
    c: PointOnObject(g0,g-3)
    c: Coincident(g1,g-4)
    c: PointOnObject(g2,g-5)
    c: Coincident(g4,g5)
    c: Coincident(g5,g6)
    c: Coincident(g6,g7)
    c: Coincident(g7,g4)
    c: Horizontal(g4)
    c: Horizontal(g6)
    c: Vertical(g5)
    c: Vertical(g7)
    c: PointOnObject(g4,g1)
    c: PointOnObject(g4,g-6)
    c: PointOnObject(g5,g-6)
    c: DistanceY(g5) = -2
    c: Coincident(g8,g4)
    c: Coincident(g9,g5)
    c: PointOnObject(g9,g3)
    c: PointOnObject(g9,g6)
    c: PointOnObject(g8,g3)
    c: PointOnObject(g8,g4)
    c: Coincident(g10,g8)
    c: Coincident(g10,g2)
    c: Coincident(g11,g9)
    c: Coincident(g11,g0)
FEATURE [PartDesign::Pad] Pad008
  Length = 2
  Length2 = 100
  Profile = -> Sketch044
  Reversed = true
  Type = 0
FEATURE [Sketcher::SketchObject] Sketch045
  ExternalGeometry = -> [Pad008]
  MapMode = 5
  Placement = pos=(0,0,8) rot=(1,0,0;3.14159rad)
  Support = -> [Pad008]
  sketch-geometry (2):
    g0: Circle CenterX=4.6 CenterY=-38 CenterZ=0 NormalX=0 NormalY=0 NormalZ=1 Radius=4.8
    g1: Circle CenterX=4.6 CenterY=-38 CenterZ=0 NormalX=0 NormalY=0 NormalZ=1 Radius=4.4
  constraints (4):
    c: Coincident(g0,g-3)
    c: Coincident(g1,g0)
    c: Radius(g1) = 4.4
    c: Radius(g0) = 4.8
FEATURE [PartDesign::Pad] Pad009
  Length = 8
  Length2 = 100
  Profile = -> Sketch045
  Type = 0
FEATURE [Sketcher::SketchObject] Sketch046
  ExternalGeometry = -> [Pad009]
  MapMode = 5
  Placement = pos=(0,0,8) rot=(1,0,0;3.14159rad)
  Support = -> [Pad009]
  sketch-geometry (5):
    g0: LineSegment StartX=-6.5 StartY=-34.2 StartZ=0 EndX=-6.1 EndY=-34.2 EndZ=0
    g1: LineSegment StartX=-6.1 StartY=-34.2 StartZ=0 EndX=-6.1 EndY=-41.8 EndZ=0
    g2: LineSegment StartX=-6.1 StartY=-41.8 StartZ=0 EndX=-6.5 EndY=-41.8 EndZ=0
    g3: LineSegment StartX=-6.5 StartY=-41.8 StartZ=0 EndX=-6.5 EndY=-34.2 EndZ=0
    g4: LineSegment [constr] StartX=4.6 StartY=-38 StartZ=0 EndX=-6.5 EndY=-38 EndZ=0
  constraints (15):
    c: Coincident(g0,g1)
    c: Coincident(g1,g2)
    c: Coincident(g2,g3)
    c: Coincident(g3,g0)
    c: Horizontal(g0)
    c: Horizontal(g2)
    c: Vertical(g1)
    c: Vertical(g3)
    c: PointOnObject(g0,g-3)
    c: Coincident(g4,g-4)
    c: PointOnObject(g4,g3)
    c: Horizontal(g4)
    c: Symmetric(g0,g2,g4)
    c: DistanceX(g0) = 0.4
    c: DistanceY(g1) = -7.6
FEATURE [PartDesign::Pad] Pad010
  Length = 8
  Length2 = 100
  Profile = -> Sketch046
  Type = 0
FEATURE [Sketcher::SketchObject] Sketch047
  ExternalGeometry = -> [Pad010]
  MapMode = 5
  Placement = pos=(0,0,0) rot=(1,0,0;3.14159rad)
  Support = -> [Pad010]
  sketch-geometry (5):
    g0: LineSegment StartX=-6.5 StartY=-36.5 StartZ=0 EndX=14.4 EndY=-36.5 EndZ=0
    g1: LineSegment StartX=14.4 StartY=-36.5 StartZ=0 EndX=14.4 EndY=-39.5 EndZ=0
    g2: LineSegment StartX=14.4 StartY=-39.5 StartZ=0 EndX=-6.5 EndY=-39.5 EndZ=0
    g3: LineSegment StartX=-6.5 StartY=-39.5 StartZ=0 EndX=-6.5 EndY=-36.5 EndZ=0
    g4: LineSegment [constr] StartX=-6.5 StartY=-38 StartZ=0 EndX=4.6 EndY=-38 EndZ=0
  constraints (15):
    c: Coincident(g0,g1)
    c: Coincident(g1,g2)
    c: Coincident(g2,g3)
    c: Coincident(g3,g0)
    c: Horizontal(g0)
    c: Horizontal(g2)
    c: Vertical(g1)
    c: Vertical(g3)
    c: PointOnObject(g0,g-4)
    c: Coincident(g4,g-3)
    c: Horizontal(g4)
    c: PointOnObject(g4,g-4)
    c: Symmetric(g0,g2,g4)
    c: DistanceY(g1) = -3
    c: DistanceX(g4,g1) = 9.8
FEATURE [PartDesign::Pad] Pad011
  Length = 2
  Length2 = 100
  Profile = -> Sketch047
  Reversed = true
  Type = 0
FEATURE [Part::Feature] Pad011001  label="Pad012"
  shape: bbox 97.06 x 64.55 x 28 mm, 206 faces (baked)
FEATURE [Sketcher::SketchObject] Sketch048
  ExternalGeometry = -> [Pad011001]
  MapMode = 5
  Placement = pos=(0,0,0) rot=(1,0,0;3.14159rad)
  Support = -> [Pad011001]
  sketch-geometry (2):
    g0: Circle CenterX=4.6 CenterY=-38 CenterZ=0 NormalX=0 NormalY=0 NormalZ=1 Radius=6.2
    g1: Circle CenterX=4.6 CenterY=-38 CenterZ=0 NormalX=0 NormalY=0 NormalZ=1 Radius=6.6
  constraints (4):
    c: Coincident(g0,g-3)
    c: Radius(g0) = 6.2
    c: Coincident(g1,g0)
    c: Radius(g1) = 6.6
FEATURE [PartDesign::Pad] Pad011002
  Length = 7.6
  Length2 = 100
  Profile = -> Sketch048
  Reversed = true
  Type = 0
FEATURE [Sketcher::SketchObject] Sketch049
  ExternalGeometry = -> [Pad011002]
  MapMode = 5
  Placement = pos=(0,0,0) rot=(1,0,0;3.14159rad)
  Support = -> [Pad011002]
  sketch-geometry (2):
    g0: Circle CenterX=4.6 CenterY=-38 CenterZ=0 NormalX=0 NormalY=0 NormalZ=1 Radius=8
    g1: Circle CenterX=4.6 CenterY=-38 CenterZ=0 NormalX=0 NormalY=0 NormalZ=1 Radius=8.4
  constraints (4):
    c: Coincident(g0,g-3)
    c: Radius(g0) = 8
    c: Coincident(g1,g0)
    c: Radius(g1) = 8.4
FEATURE [PartDesign::Pad] Pad011003
  Length = 7.6
  Length2 = 100
  Profile = -> Sketch049
  Reversed = true
  Type = 0
FEATURE [Sketcher::SketchObject] Sketch050
  ExternalGeometry = -> [Pad011003]
  MapMode = 5
  Placement = pos=(0,0,0) rot=(1,0,0;3.14159rad)
  Support = -> [Pad011003]
  sketch-geometry (2):
    g0: Circle CenterX=4.6 CenterY=-38 CenterZ=0 NormalX=0 NormalY=0 NormalZ=1 Radius=10.2
    g1: Circle CenterX=4.6 CenterY=-38 CenterZ=0 NormalX=0 NormalY=0 NormalZ=1 Radius=9.8
  constraints (4):
    c: Coincident(g0,g-3)
    c: Radius(g0) = 10.2
    c: Coincident(g1,g0)
    c: Radius(g1) = 9.8
FEATURE [PartDesign::Pad] Pad011004
  Length = 7.6
  Length2 = 100
  Profile = -> Sketch050
  Reversed = true
  Type = 0
FEATURE [Part::Feature] Pad011004001  label="Pad011005"
  shape: bbox 97.06 x 64.55 x 28 mm, 229 faces (baked)
FEATURE [Sketcher::SketchObject] Sketch051
  ExternalGeometry = -> [Pad011004001]
  MapMode = 5
  Placement = pos=(0,0,0) rot=(1,0,0;3.14159rad)
  Support = -> [Pad011004001]
  sketch-geometry (1):
    g0: Circle CenterX=4.6 CenterY=-38 CenterZ=0 NormalX=0 NormalY=0 NormalZ=1 Radius=4.4
  constraints (2):
    c: Coincident(g0,g-3)
    c: PointOnObject(g-3,g0)
FEATURE [PartDesign::Pocket] Pocket032002
  Length = 2
  Profile = -> Sketch051
  Type = 0
FEATURE [Part::Feature] Pocket032002001  label="Pocket032003"
  shape: bbox 97.14 x 64.63 x 28.08 mm, 229 faces (baked)
FEATURE [Sketcher::SketchObject] Sketch052
  ExternalGeometry = -> [Pocket032002001]
  MapMode = 5
  Placement = pos=(0,-1.35e-10,0) rot=(1,0,0;1.5708rad)
  Support = -> [Pocket032002001]
  sketch-geometry (17):
    g0: ArcOfCircle CenterX=-31.5 CenterY=24.5 CenterZ=0 NormalX=0 NormalY=0 NormalZ=1 Radius=3.5 StartAngle=1.5708 EndAngle=3.14159
    g1: ArcOfCircle CenterX=-31.5 CenterY=3.5 CenterZ=0 NormalX=0 NormalY=0 NormalZ=1 Radius=3.5 StartAngle=3.14159 EndAngle=4.71239
    g2: ArcOfCircle CenterX=38.5 CenterY=24.5 CenterZ=0 NormalX=0 NormalY=0 NormalZ=1 Radius=3.5 StartAngle=0 EndAngle=1.5708
    g3: LineSegment [constr] StartX=-35 StartY=24.5 StartZ=0 EndX=-31.5 EndY=24.5 EndZ=0
    g4: LineSegment [constr] StartX=-31.5 StartY=24.5 StartZ=0 EndX=-31.5 EndY=28 EndZ=0
    g5: LineSegment [constr] StartX=-35 StartY=3.5 StartZ=0 EndX=-31.5 EndY=3.5 EndZ=0
    g6: LineSegment [constr] StartX=-31.5 StartY=3.5 StartZ=0 EndX=-31.5 EndY=0 EndZ=0
    g7: LineSegment [constr] StartX=38.5 StartY=28 StartZ=0 EndX=38.5 EndY=24.5 EndZ=0
    g8: LineSegment [constr] StartX=38.5 StartY=24.5 StartZ=0 EndX=42 EndY=24.5 EndZ=0
    g9: LineSegment StartX=-31.5 StartY=28 StartZ=0 EndX=38.5 EndY=28 EndZ=0
    g10: LineSegment StartX=-35 StartY=24.5 StartZ=0 EndX=-35 EndY=3.5 EndZ=0
    g11: LineSegment StartX=-31.5 StartY=0 StartZ=0 EndX=-31.5 EndY=-5 EndZ=0
    g12: LineSegment StartX=-31.5 StartY=-5 StartZ=0 EndX=-41.5 EndY=-5 EndZ=0
    g13: LineSegment StartX=-41.5 StartY=-5 StartZ=0 EndX=-41.5 EndY=34.5 EndZ=0
    g14: LineSegment StartX=-41.5 StartY=34.5 StartZ=0 EndX=47 EndY=34.5 EndZ=0
    g15: LineSegment StartX=47 StartY=34.5 StartZ=0 EndX=47 EndY=24.5 EndZ=0
    g16: LineSegment StartX=42 StartY=24.5 StartZ=0 EndX=47 EndY=24.5 EndZ=0
  constraints (47):
    c: Coincident(g3,g0)
    c: Horizontal(g3)
    c: DistanceX(g3) = 3.5
    c: Coincident(g3,g0)
    c: Coincident(g4,g0)
    c: Coincident(g4,g0)
    c: Vertical(g4)
    c: Coincident(g5,g1)
    c: Coincident(g5,g1)
    c: Horizontal(g5)
    c: Coincident(g6,g1)
    c: Vertical(g6)
    c: DistanceX(g5) = 3.5
    c: Coincident(g7,g2)
    c: Vertical(g7)
    c: Coincident(g2,g7)
    c: Coincident(g8,g2)
    c: Coincident(g8,g2)
    c: Horizontal(g8)
    c: DistanceX(g8) = 3.5
    c: Coincident(g9,g0)
    c: Coincident(g9,g2)
    c: Horizontal(g9)
    c: Coincident(g10,g0)
    c: Vertical(g10)
    c: Coincident(g1,g6)
    c: PointOnObject(g1,g-1)
    c: Coincident(g0,g-4)
    c: Coincident(g10,g1)
    c: Coincident(g2,g-4)
    c: Coincident(g11,g1)
    c: Vertical(g11)
    c: Horizontal(g12)
    c: DistanceY(g11) = -5
    c: Coincident(g11,g12)
    c: DistanceX(g12) = -10
    c: Coincident(g13,g12)
    c: Vertical(g13)
    c: DistanceY(g0,g13) = 10
    c: Coincident(g14,g13)
    c: Horizontal(g14)
    c: Coincident(g15,g14)
    c: Vertical(g15)
    c: Coincident(g16,g2)
    c: Coincident(g16,g15)
    c: Horizontal(g16)
    c: DistanceX(g16) = 5
FEATURE [PartDesign::Pocket] Pocket032002002
  Length = 8
  Profile = -> Sketch052
  Type = 0
FEATURE [Sketcher::SketchObject] Sketch053
  ExternalGeometry = -> [Pocket032002002]
  MapMode = 5
  Placement = pos=(0,0,28) rot=(0,0,1;0rad)
  Support = -> [Pocket032002002]
  sketch-geometry (1):
    g0: Circle CenterX=-12.5 CenterY=21.75 CenterZ=0 NormalX=0 NormalY=0 NormalZ=1 Radius=8.3
  constraints (3):
    c: Radius(g0) = 8.3
    c: DistanceX(g0,g-4) = 6
    c: DistanceY(g0,g-3) = -14.75
FEATURE [PartDesign::Pocket] Pocket032002003
  Length = 7.75
  Profile = -> Sketch053
  Type = 0
FEATURE [PartDesign::Fillet] Fillet001
  Base = -> Pocket032002003 [Edge388]
  Radius = 1
FEATURE [PartDesign::Fillet] Fillet002
  Base = -> Fillet001 [Edge79]
  Radius = 8
FEATURE [Part::Feature] Fillet002001  label="Fillet003"
  shape: bbox 97.14 x 64.63 x 28.55 mm, 235 faces (baked)
FEATURE [Sketcher::SketchObject] Sketch054
  ExternalGeometry = -> [Fillet002001]
  MapMode = 5
  Placement = pos=(0,0,0) rot=(1,0,0;3.14159rad)
  Support = -> [Fillet002001]
  sketch-geometry (4):
    g0: ArcOfCircle CenterX=47.2887 CenterY=-37.492 CenterZ=0 NormalX=0 NormalY=0 NormalZ=1 Radius=16.3 StartAngle=1.87918 EndAngle=5.09979
    g1: ArcOfCircle CenterX=47.2887 CenterY=-37.492 CenterZ=0 NormalX=0 NormalY=0 NormalZ=1 Radius=15 StartAngle=1.87918 EndAngle=5.09979
    g2: LineSegment StartX=52.9555 StartY=-51.3804 StartZ=0 EndX=53.4466 EndY=-52.5841 EndZ=0
    g3: LineSegment StartX=42.3414 StartY=-21.9609 StartZ=0 EndX=42.7359 EndY=-23.1996 EndZ=0
  constraints (12):
    c: Coincident(g0,g-3)
    c: Coincident(g1,g0)
    c: Radius(g1) = 15
    c: Coincident(g2,g0)
    c: PointOnObject(g-3,g2)
    c: Perpendicular(g1,g2)
    c: Coincident(g2,g1)
    c: Coincident(g3,g1)
    c: PointOnObject(g-3,g3)
    c: Perpendicular(g3,g1)
    c: Radius(g0) = 16.3
    c: Coincident(g0,g3)
FEATURE [PartDesign::Pad] Pad011004002
  Length = 9.5
  Length2 = 100
  Profile = -> Sketch054
  Reversed = true
  Type = 0
FEATURE [Part::Feature] Pad011004002001  label="Pad011004003"
  shape: bbox 97.14 x 64.63 x 28.55 mm, 236 faces (baked)
FEATURE [Sketcher::SketchObject] Sketch055
  ExternalGeometry = -> [Pad011004002001]
  MapMode = 5
  Placement = pos=(0,0,0) rot=(1,0,0;3.14159rad)
  Support = -> [Pad011004002001]
  sketch-geometry (7):
    g0: ArcOfCircle CenterX=41 CenterY=-17.75 CenterZ=0 NormalX=0 NormalY=0 NormalZ=1 Radius=5.71942 StartAngle=5.02077 EndAngle=6.62856
    g1: ArcOfCircle CenterX=41 CenterY=-17.75 CenterZ=0 NormalX=0 NormalY=0 NormalZ=1 Radius=4.21841 StartAngle=5.02077 EndAngle=6.51178
    g2: LineSegment StartX=46.3817 StartY=-15.8137 StartZ=0 EndX=42.1336 EndY=-4.00682 EndZ=0
    g3: LineSegment StartX=45.1087 StartY=-16.7941 StartZ=0 EndX=42.1336 EndY=-4.00682 EndZ=0
    g4: LineSegment StartX=42.7359 StartY=-23.1996 StartZ=0 EndX=40.8511 EndY=-22.2247 EndZ=0
    g5: LineSegment StartX=42.2804 StartY=-21.7694 StartZ=0 EndX=40.8511 EndY=-22.2247 EndZ=0
    g6: LineSegment [constr] StartX=42.2804 StartY=-21.7694 StartZ=0 EndX=42.7359 EndY=-23.1996 EndZ=0
  constraints (19):
    c: Coincident(g0,g-3)
    c: Coincident(g0,g-4)
    c: Coincident(g1,g0)
    c: Coincident(g2,g0)
    c: PointOnObject(g2,g-5)
    c: Coincident(g3,g1)
    c: Coincident(g3,g2)
    c: Distance(g2,g-5) = 13
    c: Tangent(g3,g1)
    c: Tangent(g0,g2)
    c: Coincident(g4,g0)
    c: Coincident(g5,g1)
    c: Coincident(g5,g4)
    c: Tangent(g5,g1)
    c: Coincident(g6,g1)
    c: Coincident(g6,g0)
    c: Perpendicular(g6,g0)
    c: Distance(g5) = 1.5
    c: Distance(g6) = 1.50101
FEATURE [PartDesign::Pad] Pad011004002002
  Length = 9.5
  Length2 = 100
  Profile = -> Sketch055
  Reversed = true
  Type = 0
FEATURE [Part::Feature] Pad011004002002001  label="Pad011004002003"
  shape: bbox 97.14 x 64.63 x 28.55 mm, 236 faces (baked)
FEATURE [Sketcher::SketchObject] Sketch056
  ExternalGeometry = -> [Pad011004002002001]
  MapMode = 5
  Placement = pos=(0,0,6.8e-11) rot=(1,0,0;3.14159rad)
  Support = -> [Pad011004002002001]
  sketch-geometry (5):
    g0: ArcOfCircle CenterX=55.547 CenterY=-57.7318 CenterZ=0 NormalX=0 NormalY=0 NormalZ=1 Radius=6.85971 StartAngle=5.09979 EndAngle=8.24138
    g1: LineSegment StartX=52.9555 StartY=-51.3804 StartZ=0 EndX=50.4411 EndY=-53.8947 EndZ=0
    g2: LineSegment StartX=50.4411 StartY=-53.8947 StartZ=0 EndX=59.6411 EndY=-53.8947 EndZ=0
    g3: LineSegment StartX=58.1385 StartY=-64.0831 StartZ=0 EndX=59.6411 EndY=-60.5481 EndZ=0
    g4: LineSegment StartX=59.6411 StartY=-53.8947 StartZ=0 EndX=59.6411 EndY=-60.5481 EndZ=0
  constraints (15):
    c: PointOnObject(g0,g-3)
    c: Tangent(g0,g-3)
    c: Coincident(g-4,g0)
    c: Tangent(g0,g-5)
    c: Coincident(g1,g0)
    c: Coincident(g2,g1)
    c: Horizontal(g2)
    c: Angle(g2,g1) = 0.785398
    c: Distance(g2) = 9.2
    c: Coincident(g3,g0)
    c: Coincident(g4,g2)
    c: Coincident(g4,g3)
    c: Vertical(g4)
    c: Distance(g1) = 3.55581
    c: Distance(g4) = 6.65332
FEATURE [PartDesign::Pad] Pad011004002002002
  Length = 9.5
  Length2 = 100
  Profile = -> Sketch056
  Reversed = true
  Type = 0
FEATURE [Part::Feature] Pad011004002002002001  label="Pad011004002002003"
  shape: bbox 97.48 x 64.63 x 28.55 mm, 236 faces (baked)
FEATURE [Sketcher::SketchObject] Sketch058
  ExternalGeometry = -> [Pad011004002002002001]
  MapMode = 5
  Placement = pos=(0,0,28) rot=(0,0,1;0rad)
  Support = -> [Pad011004002002002001]
  sketch-geometry (4):
    g0: LineSegment StartX=38.5 StartY=7 StartZ=0 EndX=42.1 EndY=7 EndZ=0
    g1: LineSegment StartX=42.1 StartY=7 StartZ=0 EndX=42.1 EndY=2.01e-10 EndZ=0
    g2: LineSegment StartX=42.1 StartY=2.01e-10 StartZ=0 EndX=38.5 EndY=2.01e-10 EndZ=0
    g3: LineSegment StartX=38.5 StartY=2.01e-10 StartZ=0 EndX=38.5 EndY=7 EndZ=0
  constraints (11):
    c: Coincident(g0,g1)
    c: Coincident(g1,g2)
    c: Coincident(g2,g3)
    c: Coincident(g3,g0)
    c: Horizontal(g0)
    c: Horizontal(g2)
    c: Vertical(g1)
    c: Vertical(g3)
    c: Coincident(g0,g-3)
    c: Coincident(g2,g-3)
    c: DistanceX(g0) = 3.6
FEATURE [PartDesign::Pad] Pad011004002002002002
  Length = 28
  Length2 = 100
  Profile = -> Sketch058
  Reversed = true
  Type = 0
FEATURE [Sketcher::SketchObject] Sketch059
  ExternalGeometry = -> [Pad011004002002002002]
  MapMode = 5
  Placement = pos=(0,0,0) rot=(1,0,0;3.14159rad)
  Support = -> [Pad011004002002002002]
  sketch-geometry (4):
    g0: ArcOfCircle CenterX=38.5 CenterY=-3.5 CenterZ=0 NormalX=0 NormalY=0 NormalZ=1 Radius=3.5 StartAngle=0.327618 EndAngle=1.5708
    g1: LineSegment StartX=46.3817 StartY=-15.8137 StartZ=0 EndX=41.8138 EndY=-2.37374 EndZ=0
    g2: LineSegment StartX=38.5 StartY=0 StartZ=0 EndX=44.3817 EndY=-15.8137 EndZ=0
    g3: LineSegment StartX=44.3817 StartY=-15.8137 StartZ=0 EndX=46.3817 EndY=-15.8137 EndZ=0
  constraints (12):
    c: Coincident(g0,g-3)
    c: Radius(g0) = 3.5
    c: PointOnObject(g0,g-4)
    c: Coincident(g1,g-6)
    c: PointOnObject(g1,g0)
    c: Coincident(g0,g1)
    c: Coincident(g2,g0)
    c: Coincident(g3,g2)
    c: Coincident(g3,g1)
    c: Horizontal(g3)
    c: DistanceX(g3) = 2
    c: Tangent(g1,g0)
FEATURE [PartDesign::Pad] Pad011004002002002003
  Length = 9.5
  Length2 = 100
  Profile = -> Sketch059
  Reversed = true
  Type = 0
FEATURE [Sketcher::SketchObject] Sketch060
  ExternalGeometry = -> [Pad011004002002002003]
  MapMode = 5
  Placement = pos=(38.5,0,0) rot=(0.57735,-0.57735,-0.57735;2.0944rad)
  Support = -> [Pad011004002002002003]
  sketch-geometry (3):
    g0: LineSegment StartX=-0.75 StartY=0 StartZ=0 EndX=-2.01e-10 EndY=0.893816 EndZ=0
    g1: LineSegment StartX=-2.01e-10 StartY=0.893816 StartZ=0 EndX=-2.01e-10 EndY=0 EndZ=0
    g2: LineSegment StartX=-2.01e-10 StartY=0 StartZ=0 EndX=-0.75 EndY=0 EndZ=0
  constraints (7):
    c: Coincident(g1,g0)
    c: Vertical(g1)
    c: Coincident(g2,g1)
    c: Coincident(g2,g0)
    c: Horizontal(g2)
    c: Coincident(g0,g-3)
    c: Coincident(g0,g-3)
FEATURE [PartDesign::Pocket] Pocket032002004  label="Pocket036"
  Length = 5
  Profile = -> Sketch060
  Type = 0
FEATURE [Part::Feature] Pocket032002004001  label="Pocket032002004"
  shape: bbox 97.48 x 64.63 x 28.55 mm, 232 faces (baked)
FEATURE [Sketcher::SketchObject] Sketch061
  ExternalGeometry = -> [Pocket032002004001]
  MapMode = 5
  Placement = pos=(0,0,1.01e-10) rot=(1,0,0;3.14159rad)
  Support = -> [Pocket032002004001]
  sketch-geometry (7):
    g0: ArcOfCircle CenterX=38.6 CenterY=-3.5 CenterZ=0 NormalX=0 NormalY=0 NormalZ=1 Radius=3.5 StartAngle=0.162105 EndAngle=1.5708
    g1: LineSegment [constr] StartX=38.6 StartY=3e-12 StartZ=0 EndX=38.6 EndY=-3.5 EndZ=0
    g2: LineSegment StartX=42.0541 StartY=-2.93512 StartZ=0 EndX=42.1 EndY=-3.21571 EndZ=0
    g3: LineSegment StartX=38.6 StartY=2 StartZ=0 EndX=44.1 EndY=2 EndZ=0
    g4: LineSegment StartX=44.1 StartY=2 StartZ=0 EndX=44.1 EndY=-3.21571 EndZ=0
    g5: LineSegment StartX=38.6 StartY=3e-12 StartZ=0 EndX=38.6 EndY=2 EndZ=0
    g6: LineSegment StartX=42.1 StartY=-3.21571 StartZ=0 EndX=44.1 EndY=-3.21571 EndZ=0
  constraints (20):
    c: PointOnObject(g0,g-3)
    c: DistanceX(g0,g-3) = 3.5
    c: Coincident(g1,g0)
    c: Coincident(g1,g0)
    c: Vertical(g1)
    c: Radius(g0) = 3.5
    c: Coincident(g2,g0)
    c: Coincident(g2,g-4)
    c: Tangent(g2,g0)
    c: Coincident(g3,g4)
    c: Horizontal(g3)
    c: Vertical(g4)
    c: Coincident(g5,g0)
    c: Coincident(g5,g3)
    c: Vertical(g5)
    c: Coincident(g6,g2)
    c: Coincident(g6,g4)
    c: Horizontal(g6)
    c: DistanceX(g6) = 2
    c: DistanceY(g5) = 2
FEATURE [PartDesign::Pocket] Pocket032002004002
  Length = 28
  Profile = -> Sketch061
  Type = 0
FEATURE [PartDesign::Fillet] Fillet002002
  Base = -> Pocket032002004002 [Edge178]
  Radius = 3.5
FEATURE [Sketcher::SketchObject] Sketch062
  ExternalGeometry = -> [Fillet002002]
  MapMode = 5
  Placement = pos=(0,8.4e-11,0) rot=(1,0,0;1.5708rad)
  Support = -> [Fillet002002]
  sketch-geometry (5):
    g0: ArcOfCircle CenterX=36.1 CenterY=22 CenterZ=0 NormalX=0 NormalY=0 NormalZ=1 Radius=6 StartAngle=0 EndAngle=1.5708
    g1: LineSegment StartX=36.1 StartY=30 StartZ=0 EndX=44.1 EndY=30 EndZ=0
    g2: LineSegment StartX=44.1 StartY=30 StartZ=0 EndX=44.1 EndY=22 EndZ=0
    g3: LineSegment StartX=36.1 StartY=30 StartZ=0 EndX=36.1 EndY=28 EndZ=0
    g4: LineSegment StartX=42.1 StartY=22 StartZ=0 EndX=44.1 EndY=22 EndZ=0
  constraints (16):
    c: Coincident(g1,g2)
    c: Horizontal(g1)
    c: Vertical(g2)
    c: Coincident(g3,g1)
    c: Coincident(g3,g0)
    c: Vertical(g3)
    c: Coincident(g4,g0)
    c: Coincident(g4,g2)
    c: Horizontal(g4)
    c: Radius(g0) = 6
    c: PointOnObject(g0,g4)
    c: PointOnObject(g0,g3)
    c: PointOnObject(g0,g-3)
    c: PointOnObject(g0,g-4)
    c: DistanceY(g3) = -2
    c: DistanceX(g4) = 2
FEATURE [PartDesign::Pocket] Pocket032002004003
  Length = 8
  Profile = -> Sketch062
  Type = 0
FEATURE [Sketcher::SketchObject] Sketch064
  MapMode = 5
  Placement = pos=(0,8.4e-11,0) rot=(1,0,0;1.5708rad)
  sketch-geometry (4):
    g0: LineSegment StartX=-6.02622 StartY=19.9946 StartZ=0 EndX=-2.50003 EndY=23.5394 EndZ=0
    g1: LineSegment StartX=-2.50003 StartY=23.5394 StartZ=0 EndX=2.49997 EndY=23.5394 EndZ=0
    g2: LineSegment StartX=2.49997 StartY=23.5394 StartZ=0 EndX=6.02622 EndY=19.9946 EndZ=0
    g3: ArcOfCircle CenterX=0 CenterY=14.018 CenterZ=0 NormalX=0 NormalY=0 NormalZ=1 Radius=8.48734 StartAngle=2.36033 EndAngle=7.06445
  constraints (5):
    c: Horizontal(g1)
    c: Coincident(g2,g1)
    c: PointOnObject(g3,g-2)
    c: Coincident(g3,g2)
    c: Coincident(g3,g0)
FEATURE [Sketcher::SketchObject] Sketch065
  MapMode = 5
  Placement = pos=(0,8.4e-11,0) rot=(1,0,0;1.5708rad)
  Support = -> [Pocket032002004003]
  sketch-geometry (4):
    g0: ArcOfCircle CenterX=0 CenterY=14.0158 CenterZ=0 NormalX=0 NormalY=0 NormalZ=1 Radius=8.5437 StartAngle=2.37091 EndAngle=7.06488
    g1: LineSegment StartX=-6.12956 StartY=19.9676 StartZ=0 EndX=-2.51381 EndY=23.5833 EndZ=0
    g2: LineSegment StartX=6.06363 StartY=20.0347 StartZ=0 EndX=2.51504 EndY=23.5833 EndZ=0
    g3: LineSegment StartX=2.51504 StartY=23.5833 StartZ=0 EndX=-2.51381 EndY=23.5833 EndZ=0
  constraints (8):
    c: PointOnObject(g0,g-2)
    c: Coincident(g1,g0)
    c: Coincident(g2,g0)
    c: Coincident(g3,g2)
    c: Coincident(g3,g1)
    c: Horizontal(g3)
    c: Angle(g1) = 0.785398
    c: Angle(g2) = 2.35619
FEATURE [PartDesign::Pocket] Pocket032002004004
  Length = 4.338
  Profile = -> Sketch065
  Type = 0
FEATURE [Sketcher::SketchObject] Sketch066
  MapMode = 5
  Placement = pos=(-7e-12,4.338,1.5e-11) rot=(1,0,0;1.5708rad)
  Support = -> [Pocket032002004004]
  sketch-geometry (4):
    g0: ArcOfCircle CenterX=0 CenterY=13.9318 CenterZ=0 NormalX=0 NormalY=0 NormalZ=1 Radius=3.25 StartAngle=2.32888 EndAngle=7.08544
    g1: LineSegment StartX=-0.976959 StartY=17.5493 StartZ=0 EndX=0.97802 EndY=17.5493 EndZ=0
    g2: LineSegment StartX=-0.976959 StartY=17.5493 StartZ=0 EndX=-2.23448 EndY=16.2918 EndZ=0
    g3: LineSegment StartX=0.97802 StartY=17.5493 StartZ=0 EndX=2.25903 EndY=16.2683 EndZ=0
  constraints (4):
    c: Horizontal(g1)
    c: Coincident(g2,g0)
    c: Coincident(g3,g1)
    c: Coincident(g3,g0)
FEATURE [PartDesign::Pocket] Pocket032002004005
  Length = 0.5
  Profile = -> Sketch066
  Type = 0
FEATURE [Sketcher::SketchObject] Sketch067
  MapMode = 5
  Placement = pos=(0,0,18.3) rot=(0,0,1;0rad)
  Support = -> [Pocket032002004005]
  sketch-geometry (6):
    g0: LineSegment StartX=15.7 StartY=55.825 StartZ=0 EndX=13.9 EndY=55.825 EndZ=0
    g1: LineSegment StartX=13.9 StartY=55.825 StartZ=0 EndX=13.9 EndY=62 EndZ=0
    g2: LineSegment StartX=13.9 StartY=62 StartZ=0 EndX=10.2 EndY=62 EndZ=0
    g3: LineSegment StartX=10.2 StartY=62 StartZ=0 EndX=10.2 EndY=50.175 EndZ=0
    g4: LineSegment StartX=10.2 StartY=50.175 StartZ=0 EndX=15.7 EndY=50.175 EndZ=0
    g5: LineSegment StartX=15.7 StartY=50.175 StartZ=0 EndX=15.7 EndY=55.825 EndZ=0
  constraints (12):
    c: Horizontal(g0)
    c: Coincident(g1,g0)
    c: Vertical(g1)
    c: Coincident(g2,g1)
    c: Horizontal(g2)
    c: Coincident(g3,g2)
    c: Vertical(g3)
    c: Coincident(g4,g3)
    c: Horizontal(g4)
    c: Coincident(g5,g4)
    c: Coincident(g5,g0)
    c: Vertical(g5)
FEATURE [PartDesign::Pad] Pad011004002002002004
  Length = 0.1
  Length2 = 100
  Profile = -> Sketch067
  Type = 0
FEATURE [Sketcher::SketchObject] Sketch068
  MapMode = 5
  Placement = pos=(0,0,1.01e-10) rot=(1,0,0;3.14159rad)
  Support = -> [Pad011004002002002004]
  sketch-geometry (4):
    g0: ArcOfCircle CenterX=4.78547 CenterY=-38.0219 CenterZ=0 NormalX=0 NormalY=0 NormalZ=1 Radius=10.6375 StartAngle=3.52487 EndAngle=9.03481
    g1: LineSegment StartX=-5.0534 StartY=-33.9781 StartZ=0 EndX=-8 EndY=-33.9781 EndZ=0
    g2: LineSegment StartX=-8 StartY=-33.9781 StartZ=0 EndX=-8 EndY=-42 EndZ=0
    g3: LineSegment StartX=-8 StartY=-42 StartZ=0 EndX=-5.08021 EndY=-42 EndZ=0
  constraints (7):
    c: Coincident(g1,g2)
    c: Coincident(g2,g3)
    c: Horizontal(g1)
    c: Horizontal(g3)
    c: Vertical(g2)
    c: Coincident(g0,g3)
    c: Coincident(g0,g1)
FEATURE [PartDesign::Pocket] Pocket032002004006
  Length = 8
  Profile = -> Sketch068
  Type = 0
  UpToFace = -> Pad011004002002002004 [Face125]
FEATURE [Sketcher::SketchObject] Sketch069
  MapMode = 5
  Placement = pos=(-1e-12,1e-12,8) rot=(1,0,0;3.14159rad)
  Support = -> [Pocket032002004006]
  sketch-geometry (2):
    g0: Circle CenterX=4.5888 CenterY=-38 CenterZ=0 NormalX=0 NormalY=0 NormalZ=1 Radius=9.5
    g1: Circle CenterX=4.5888 CenterY=-38 CenterZ=0 NormalX=0 NormalY=0 NormalZ=1 Radius=10
  constraints (2):
    c: Radius(g0) = 9.5
    c: Radius(g1) = 10
FEATURE [Sketcher::SketchObject] Sketch070
  MapMode = 5
  Placement = pos=(-1e-12,1e-12,8) rot=(1,0,0;3.14159rad)
  sketch-geometry (2):
    g0: Circle CenterX=4.6 CenterY=-38 CenterZ=0 NormalX=0 NormalY=0 NormalZ=1 Radius=7
    g1: Circle CenterX=4.6 CenterY=-38 CenterZ=0 NormalX=0 NormalY=0 NormalZ=1 Radius=7.5
  constraints (3):
    c: Radius(g0) = 7
    c: Radius(g1) = 7.5
    c: Coincident(g0,g1)
FEATURE [Sketcher::SketchObject] Sketch072
  MapMode = 5
  Placement = pos=(-1e-12,1e-12,8) rot=(1,0,0;3.14159rad)
  Support = -> [Pocket032002004006]
  sketch-geometry (4):
    g0: LineSegment StartX=-6.5 StartY=-34.2 StartZ=0 EndX=-5.70463 EndY=-34.2 EndZ=0
    g1: LineSegment StartX=-5.70463 StartY=-34.2 StartZ=0 EndX=-5.70463 EndY=-41.9771 EndZ=0
    g2: LineSegment StartX=-5.70463 StartY=-41.9771 StartZ=0 EndX=-6.5 EndY=-41.9771 EndZ=0
    g3: LineSegment StartX=-6.5 StartY=-41.9771 StartZ=0 EndX=-6.5 EndY=-34.2 EndZ=0
  constraints (8):
    c: Coincident(g0,g1)
    c: Coincident(g1,g2)
    c: Coincident(g2,g3)
    c: Coincident(g3,g0)
    c: Horizontal(g0)
    c: Horizontal(g2)
    c: Vertical(g1)
    c: Vertical(g3)
FEATURE [PartDesign::Pad] Pad011004002002002005
  Length = 10
  Length2 = 100
  Profile = -> Sketch072
  Type = 3
  UpToFace = -> Pocket032002004006 [Face19]
FEATURE [Sketcher::SketchObject] Sketch074
  MapMode = 5
  Placement = pos=(0,0,1.01e-10) rot=(1,0,0;3.14159rad)
  Support = -> [Pad011004002002002005]
  sketch-geometry (4):
    g0: LineSegment StartX=-6.40983 StartY=-35 StartZ=0 EndX=15.028 EndY=-35 EndZ=0
    g1: LineSegment StartX=15.028 StartY=-35 StartZ=0 EndX=15.028 EndY=-40.9795 EndZ=0
    g2: LineSegment StartX=15.028 StartY=-40.9795 StartZ=0 EndX=-6.40983 EndY=-40.9795 EndZ=0
    g3: LineSegment StartX=-6.40983 StartY=-40.9795 StartZ=0 EndX=-6.40983 EndY=-35 EndZ=0
  constraints (8):
    c: Coincident(g0,g1)
    c: Coincident(g1,g2)
    c: Coincident(g2,g3)
    c: Coincident(g3,g0)
    c: Horizontal(g0)
    c: Horizontal(g2)
    c: Vertical(g1)
    c: Vertical(g3)
FEATURE [PartDesign::Pad] Pad011004002002002006
  Length = 2
  Length2 = 100
  Profile = -> Sketch074
  Reversed = true
  Type = 0
FEATURE [Sketcher::SketchObject] Sketch075
  MapMode = 5
  Placement = pos=(0,0,1.01e-10) rot=(1,0,0;3.14159rad)
  Support = -> [Pad011004002002002006]
FEATURE [Sketcher::SketchObject] Sketch076
  MapMode = 5
  Placement = pos=(0,0,1.01e-10) rot=(1,0,0;3.14159rad)
  Support = -> [Pad011004002002002006]
  sketch-geometry (2):
    g0: Circle CenterX=4.6 CenterY=-38 CenterZ=0 NormalX=0 NormalY=0 NormalZ=1 Radius=4.32243
    g1: Circle CenterX=4.6 CenterY=-38 CenterZ=0 NormalX=0 NormalY=0 NormalZ=1 Radius=4.92313
  constraints (5):
    c: DistanceY(g-1,g0) = -38
    c: DistanceX(g-1,g0) = 4.6
    c: Coincident(g0,g1)
    c: Radius(g0) = 4.32243
    c: Radius(g1) = 4.92313
FEATURE [PartDesign::Pad] Pad011004002002002007
  Length = 7.92
  Length2 = 100
  Profile = -> Sketch076
  Reversed = true
  Type = 0
FEATURE [Sketcher::SketchObject] Sketch077
  MapMode = 5
  Placement = pos=(0,0,1.01e-10) rot=(1,0,0;3.14159rad)
  Support = -> [Pad011004002002002007]
  sketch-geometry (1):
    g0: Circle CenterX=4.6 CenterY=-38 CenterZ=0 NormalX=0 NormalY=0 NormalZ=1 Radius=4.32243
FEATURE [PartDesign::Pocket] Pocket032002004007
  Length = 3
  Profile = -> Sketch077
  Type = 0
FEATURE [Sketcher::SketchObject] Sketch078
  MapMode = 5
  Placement = pos=(0,0,1.01e-10) rot=(1,0,0;3.14159rad)
  Support = -> [Pocket032002004007]
  sketch-geometry (2):
    g0: Circle CenterX=4.6 CenterY=-38 CenterZ=0 NormalX=0 NormalY=0 NormalZ=1 Radius=6.88323
    g1: Circle CenterX=4.6 CenterY=-38 CenterZ=0 NormalX=0 NormalY=0 NormalZ=1 Radius=7.52901
  constraints (1):
    c: Coincident(g1,g0)
FEATURE [PartDesign::Pad] Pad011004002002002008
  Length = 7.92
  Length2 = 100
  Profile = -> Sketch078
  Reversed = true
  Type = 0
FEATURE [Sketcher::SketchObject] Sketch079
  MapMode = 5
  Placement = pos=(0,0,1.01e-10) rot=(1,0,0;3.14159rad)
  Support = -> [Pad011004002002002008]
  sketch-geometry (2):
    g0: Circle CenterX=4.6 CenterY=-38 CenterZ=0 NormalX=0 NormalY=0 NormalZ=1 Radius=10.1147
    g1: Circle CenterX=4.6 CenterY=-38 CenterZ=0 NormalX=0 NormalY=0 NormalZ=1 Radius=9.38548
  constraints (1):
    c: Coincident(g0,g1)
FEATURE [PartDesign::Pad] Pad011004002002002009
  Length = 7.92
  Length2 = 100
  Profile = -> Sketch079
  Reversed = true
  Type = 0
FEATURE [PartDesign::Chamfer] Chamfer004
  Base = -> Pad011004002002002009 [Edge596,Edge627,Edge650,Edge658,Edge683,Edge688]
  Size = 0.3
FEATURE [Sketcher::SketchObject] Sketch080
  MapMode = 5
  Placement = pos=(0,0,0.0399993) rot=(1,0,0;3.14159rad)
  Support = -> [Chamfer004]
  sketch-geometry (4):
    g0: LineSegment StartX=-7.17844 StartY=-12.3538 StartZ=0 EndX=-18.4591 EndY=-12.3538 EndZ=0
    g1: LineSegment StartX=-18.4591 StartY=-12.3538 StartZ=0 EndX=-18.4591 EndY=-28.215 EndZ=0
    g2: LineSegment StartX=-18.4591 StartY=-28.215 StartZ=0 EndX=-7.17844 EndY=-28.215 EndZ=0
    g3: LineSegment StartX=-7.17844 StartY=-28.215 StartZ=0 EndX=-7.17844 EndY=-12.3538 EndZ=0
  constraints (8):
    c: Coincident(g0,g1)
    c: Coincident(g1,g2)
    c: Coincident(g2,g3)
    c: Coincident(g3,g0)
    c: Horizontal(g0)
    c: Horizontal(g2)
    c: Vertical(g1)
    c: Vertical(g3)
FEATURE [PartDesign::Pocket] Pocket032002004008
  Length = 0
  Profile = -> Sketch080
  Type = 3
  UpToFace = -> Chamfer004 [Face37]
FEATURE [Sketcher::SketchObject] Sketch081
  MapMode = 5
  Placement = pos=(0,0,8.32) rot=(1,0,0;3.14159rad)
  Support = -> [Pocket032002004008]
  sketch-geometry (2):
    g0: Circle CenterX=-12.4778 CenterY=-21.7373 CenterZ=0 NormalX=0 NormalY=0 NormalZ=1 Radius=1.97422
    g1: Circle CenterX=-12.4778 CenterY=-21.7373 CenterZ=0 NormalX=0 NormalY=0 NormalZ=1 Radius=2.79587
  constraints (3):
    c: Coincident(g1,g0)
    c: Radius(g0) = 1.97422
    c: Radius(g1) = 2.79587
FEATURE [PartDesign::Pad] Pad011004002002002010
  Length = 10
  Length2 = 100
  Profile = -> Sketch081
  Type = 3
  UpToFace = -> Pocket032002004008 [Face35]
FEATURE [PartDesign::Chamfer] Chamfer005
  Base = -> Pad011004002002002010 [Edge532]
  Size = 0.4
FEATURE [Sketcher::SketchObject] Sketch083
  MapMode = 5
  Placement = pos=(0,0,1.01e-10) rot=(1,0,0;3.14159rad)
  Support = -> [Chamfer005]
  sketch-geometry (4):
    g0: LineSegment StartX=-7.51618 StartY=-23.7705 StartZ=0 EndX=-17.8907 EndY=-23.7705 EndZ=0
    g1: LineSegment StartX=-17.8907 StartY=-23.7705 StartZ=0 EndX=-17.8907 EndY=-19.6432 EndZ=0
    g2: LineSegment StartX=-17.8907 StartY=-19.6432 StartZ=0 EndX=-7.51618 EndY=-19.6432 EndZ=0
    g3: LineSegment StartX=-7.51618 StartY=-19.6432 StartZ=0 EndX=-7.51618 EndY=-23.7705 EndZ=0
  constraints (8):
    c: Coincident(g0,g1)
    c: Coincident(g1,g2)
    c: Coincident(g2,g3)
    c: Coincident(g3,g0)
    c: Horizontal(g0)
    c: Horizontal(g2)
    c: Vertical(g1)
    c: Vertical(g3)
FEATURE [PartDesign::Pad] Pad011004002002002011
  Length = 2
  Length2 = 100
  Profile = -> Sketch083
  Reversed = true
  Type = 0
FEATURE [Sketcher::SketchObject] Sketch082
  MapMode = 5
  Placement = pos=(0,0,1.01e-10) rot=(1,0,0;3.14159rad)
  Support = -> [Pad011004002002002011]
  sketch-geometry (8):
    g0: ArcOfCircle CenterX=-12.5002 CenterY=-21.75 CenterZ=0 NormalX=0 NormalY=0 NormalZ=1 Radius=5.24996 StartAngle=2.02284 EndAngle=4.71242
    g1: LineSegment StartX=-12.5 StartY=-27 StartZ=0 EndX=-7.5 EndY=-27 EndZ=0
    g2: LineSegment StartX=-7.5 StartY=-27 StartZ=0 EndX=-7.5 EndY=-13.4673 EndZ=0
    g3: LineSegment StartX=-7.5 StartY=-13.4673 StartZ=0 EndX=-14.7934 EndY=-17.0274 EndZ=0
    g4: ArcOfCircle CenterX=-12.5002 CenterY=-21.75 CenterZ=0 NormalX=0 NormalY=0 NormalZ=1 Radius=4.5469 StartAngle=2.03881 EndAngle=4.71759
    g5: LineSegment StartX=-14.5513 StartY=-17.6921 StartZ=0 EndX=-8.37915 EndY=-14.7842 EndZ=0
    g6: LineSegment StartX=-8.37915 StartY=-14.7842 StartZ=0 EndX=-8.37915 EndY=-26.2969 EndZ=0
    g7: LineSegment StartX=-8.37915 StartY=-26.2969 StartZ=0 EndX=-12.4765 EndY=-26.2969 EndZ=0
  constraints (13):
    c: Coincident(g1,g0)
    c: Horizontal(g1)
    c: Coincident(g2,g1)
    c: Vertical(g2)
    c: Coincident(g3,g2)
    c: Coincident(g3,g0)
    c: Coincident(g4,g0)
    c: Coincident(g6,g5)
    c: Vertical(g6)
    c: Coincident(g7,g4)
    c: Horizontal(g7)
    c: Coincident(g6,g7)
    c: Coincident(g4,g5)
FEATURE [PartDesign::Pad] Pad011004002002002012
  Length = 8.3
  Length2 = 100
  Profile = -> Sketch082
  Reversed = true
  Type = 0
  UpToFace = -> Pad011004002002002011 [Face27]
FEATURE [PartDesign::Chamfer] Chamfer006
  Base = -> Pad011004002002002012 [Edge37,Edge42,Edge47,Edge32]
  Size = 0.3
FEATURE [PartDesign::Chamfer] Chamfer007
  Base = -> Chamfer006 [Edge49,Edge50,Edge51,Edge52]
  Size = 0.2
FEATURE [Sketcher::SketchObject] Sketch084
  MapMode = 5
  Placement = pos=(0,0,1.01e-10) rot=(1,0,0;3.14159rad)
  Support = -> [Chamfer007]
  sketch-geometry (1):
    g0: Circle CenterX=-12.4652 CenterY=-21.7504 CenterZ=0 NormalX=0 NormalY=0 NormalZ=1 Radius=1.91275
FEATURE [PartDesign::Pocket] Pocket032002004009
  Length = 5
  Profile = -> Sketch084
  Type = 0
FEATURE [Sketcher::SketchObject] Sketch085
  ExternalGeometry = -> [Pocket032002004009]
  MapMode = 5
  Placement = pos=(0,7,0) rot=(0,0.707107,0.707107;3.14159rad)
  Support = -> [Pocket032002004009]
  sketch-geometry (1):
    g0: Circle CenterX=25 CenterY=14 CenterZ=0 NormalX=0 NormalY=0 NormalZ=1 Radius=6
  constraints (2):
    c: Coincident(g0,g-3)
    c: Radius(g0) = 6
FEATURE [PartDesign::Pad] Pad011004002002002013
  Length = 4
  Length2 = 100
  Profile = -> Sketch085
  Reversed = true
  Type = 0
FEATURE [Sketcher::SketchObject] Sketch086
  ExternalGeometry = -> [Pad011004002002002013]
  MapMode = 5
  Placement = pos=(0,7,0) rot=(0,0.707107,0.707107;3.14159rad)
  Support = -> [Pad011004002002002013]
  sketch-geometry (8):
    g0: LineSegment StartX=28.914 StartY=16.2598 StartZ=0 EndX=25 EndY=18.5195 EndZ=0
    g1: LineSegment StartX=25 StartY=18.5195 StartZ=0 EndX=21.086 EndY=16.2598 EndZ=0
    g2: LineSegment StartX=21.086 StartY=16.2598 StartZ=0 EndX=21.086 EndY=11.7402 EndZ=0
    g3: LineSegment StartX=21.086 StartY=11.7402 StartZ=0 EndX=25 EndY=9.48047 EndZ=0
    g4: LineSegment StartX=25 StartY=9.48047 StartZ=0 EndX=28.914 EndY=11.7402 EndZ=0
    g5: LineSegment StartX=28.914 StartY=11.7402 StartZ=0 EndX=28.914 EndY=16.2598 EndZ=0
    g6: Circle [constr] CenterX=25 CenterY=14 CenterZ=0 NormalX=0 NormalY=0 NormalZ=1 Radius=4.51953
    g7: Circle [constr] CenterX=25 CenterY=14 CenterZ=0 NormalX=0 NormalY=0 NormalZ=1 Radius=4.51953
  constraints (18):
    c: Coincident(g0,g1)
    c: Coincident(g1,g2)
    c: Coincident(g2,g3)
    c: Coincident(g3,g4)
    c: Coincident(g4,g5)
    c: Coincident(g5,g0)
    c: Equal(g0, g1-g5) x5
    c: PointOnObject(g0,g6)
    c: PointOnObject(g1,g6)
    c: PointOnObject(g2,g6)
    c: PointOnObject(g3,g6)
    c: PointOnObject(g4,g6)
    c: PointOnObject(g5,g6)
    c: Coincident(g6,g-3)
    c: Coincident(g7,g6)
    c: PointOnObject(g-6,g7)
    c: Vertical(g5)
    c: Equal(g7,g6)
FEATURE [PartDesign::Pocket] Pocket032002004010
  Length = 3.5
  Profile = -> Sketch086
  Type = 0
FEATURE [Sketcher::SketchObject] Sketch087
  ExternalGeometry = -> [Pocket032002004010]
  MapMode = 5
  Placement = pos=(0,7,0) rot=(0,0.707107,0.707107;3.14159rad)
  Support = -> [Pocket032002004010]
  sketch-geometry (1):
    g0: Circle CenterX=25 CenterY=14 CenterZ=0 NormalX=0 NormalY=0 NormalZ=1 Radius=2.35
  constraints (2):
    c: Coincident(g0,g-4)
    c: Equal(g-4,g0)
FEATURE [PartDesign::Pocket] Pocket032002004011
  Length = 5
  Profile = -> Sketch087
  Type = 1
FEATURE [Part::Feature] Pocket032002004011001  label="Pocket032002004012"
  shape: bbox 97.49 x 64.64 x 28.56 mm, 272 faces (baked)
FEATURE [Sketcher::SketchObject] Sketch088
  ExternalGeometry = -> [Pocket032002004011001]
  MapMode = 5
  Placement = pos=(0,62,0) rot=(0,0.707107,0.707107;3.14159rad)
  Support = -> [Pocket032002004011001]
  sketch-geometry (7):
    g0: LineSegment StartX=-27.3516 StartY=18.073 StartZ=0 EndX=-29.7031 EndY=14 EndZ=0
    g1: LineSegment StartX=-29.7031 StartY=14 StartZ=0 EndX=-27.3516 EndY=9.92699 EndZ=0
    g2: LineSegment StartX=-27.3516 StartY=9.92699 StartZ=0 EndX=-22.6484 EndY=9.92699 EndZ=0
    g3: LineSegment StartX=-22.6484 StartY=9.92699 StartZ=0 EndX=-20.2969 EndY=14 EndZ=0
    g4: LineSegment StartX=-20.2969 StartY=14 StartZ=0 EndX=-22.6484 EndY=18.073 EndZ=0
    g5: LineSegment StartX=-22.6484 StartY=18.073 StartZ=0 EndX=-27.3516 EndY=18.073 EndZ=0
    g6: Circle [constr] CenterX=-25 CenterY=14 CenterZ=0 NormalX=0 NormalY=0 NormalZ=1 Radius=4.70311
  constraints (16):
    c: Coincident(g0,g1)
    c: Coincident(g1,g2)
    c: Coincident(g2,g3)
    c: Coincident(g3,g4)
    c: Coincident(g4,g5)
    c: Coincident(g5,g0)
    c: Equal(g0, g1-g5) x5
    c: PointOnObject(g0,g6)
    c: PointOnObject(g1,g6)
    c: PointOnObject(g2,g6)
    c: PointOnObject(g3,g6)
    c: PointOnObject(g4,g6)
    c: PointOnObject(g5,g6)
    c: Coincident(g6,g-3)
    c: Horizontal(g5)
    c: DistanceX(g-10,g3) = 0.5
FEATURE [PartDesign::Pocket] Pocket032002004011002
  Length = 58.5
  Profile = -> Sketch088
  Type = 0
